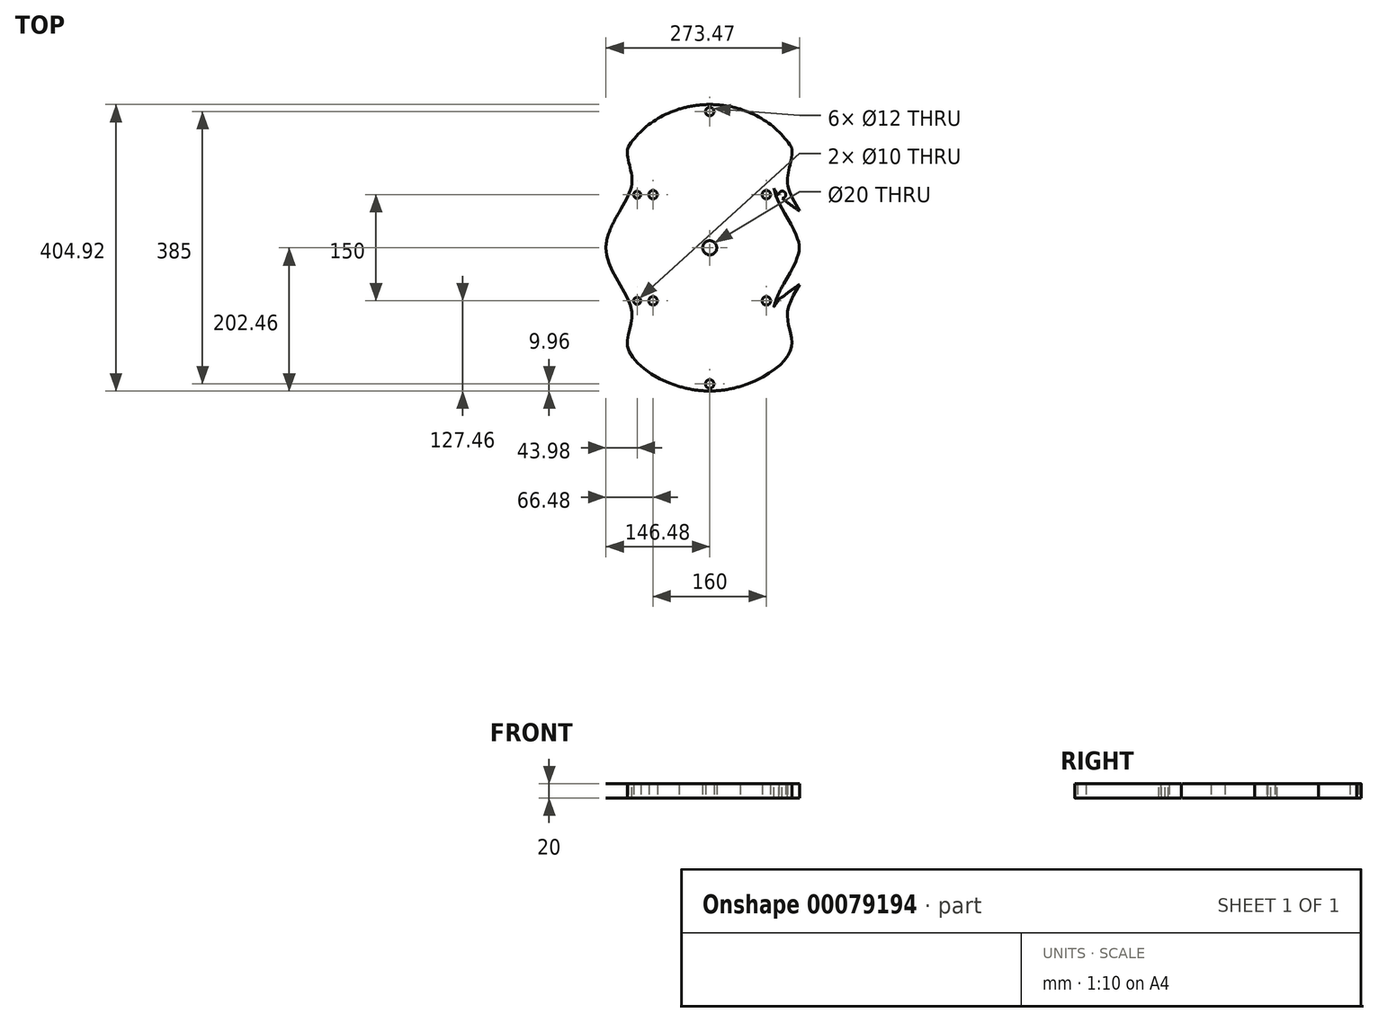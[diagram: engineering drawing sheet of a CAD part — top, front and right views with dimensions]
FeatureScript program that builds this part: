
annotation { "Feature Type Name" : "Feature", "Feature Type Description" : "" }
export const myFeature = defineFeature(function(context is Context, id is Id, definition is map)
    precondition{}
    {
        {
            var Q0;
            Q0=qCreatedBy(makeId("Top.planeOp"),FACE);
            var sketch = newSketch(context, id + "F0", { "sketchPlane" : qUnion([Q0])});
            skPoint(sketch, "E0", {"position": v(150.32, -165.76) * mm});
            skPoint(sketch, "E1", {"position": v(107.37, -221.56) * mm});
            skPoint(sketch, "E2", {"position": v(69.02, -211.72) * mm});
            skPoint(sketch, "E3", {"position": v(0, -246.18) * mm});
            skPoint(sketch, "E4", {"position": v(138.05, -177.25) * mm});
            skPoint(sketch, "E5", {"position": v(146.48, 0) * mm});
            skPoint(sketch, "E6", {"position": v(132.68, -82.88) * mm});
            skLineSegment(sketch, "E7", {"start": v(0, 292) * mm, "end": v(0, -246.18) * mm, "construction": true});
            skPoint(sketch, "E8.MirrorP", {"position": v(-146.48, 0) * mm});
            skPoint(sketch, "E9.MirrorP", {"position": v(-132.68, -82.88) * mm});
            skPoint(sketch, "E10.MirrorP", {"position": v(-150.32, -165.76) * mm});
            skPoint(sketch, "E11.MirrorP", {"position": v(-138.05, -177.25) * mm});
            skPoint(sketch, "E12.MirrorP", {"position": v(-107.37, -221.56) * mm});
            skPoint(sketch, "E13.MirrorP", {"position": v(-69.02, -211.72) * mm});
            skPoint(sketch, "E14", {"position": v(0, 0) * mm});
            skPoint(sketch, "E15", {"position": v(-146.25, -161.4) * mm});
            skPoint(sketch, "E16", {"position": v(-136.87, -189.28) * mm});
            skPoint(sketch, "E17", {"position": v(-146.26, -172.33) * mm});
            skPoint(sketch, "E18", {"position": v(-131.04, -210.06) * mm});
            skPoint(sketch, "E19", {"position": v(-94.82, -218.38) * mm});
            skPoint(sketch, "E20", {"position": v(-60.59, -222.84) * mm});
            skPoint(sketch, "E21", {"position": v(-67.25, -214.49) * mm});
            skPoint(sketch, "E22", {"position": v(-72.48, -210.2) * mm});
            skPoint(sketch, "E23", {"position": v(-119.37, -219.05) * mm});
            skPoint(sketch, "E24", {"position": v(-149.89, -167.68) * mm});
            skPoint(sketch, "E25.MirrorP", {"position": v(60.59, -222.84) * mm});
            skPoint(sketch, "E26.MirrorP", {"position": v(67.25, -214.49) * mm});
            skPoint(sketch, "E27.MirrorP", {"position": v(72.48, -210.2) * mm});
            skPoint(sketch, "E28.MirrorP", {"position": v(94.82, -218.38) * mm});
            skPoint(sketch, "E29.MirrorP", {"position": v(119.37, -219.05) * mm});
            skPoint(sketch, "E30.MirrorP", {"position": v(136.87, -189.28) * mm});
            skPoint(sketch, "E31.MirrorP", {"position": v(146.26, -172.33) * mm});
            skPoint(sketch, "E32.MirrorP", {"position": v(149.89, -167.68) * mm});
            skPoint(sketch, "E33.MirrorP", {"position": v(146.25, -161.4) * mm});
            skPoint(sketch, "E34", {"position": v(-139.73, -175.31) * mm});
            skPoint(sketch, "E35.MirrorP", {"position": v(131.04, -210.06) * mm});
            skPoint(sketch, "E36.MirrorP", {"position": v(-132.68, 82.88) * mm});
            skPoint(sketch, "E37.MirrorP", {"position": v(-139.73, 175.31) * mm});
            skPoint(sketch, "E38.MirrorP", {"position": v(-150.32, 165.76) * mm});
            skPoint(sketch, "E39.MirrorP", {"position": v(69.02, 211.72) * mm});
            skPoint(sketch, "E40.MirrorP", {"position": v(150.32, 165.76) * mm});
            skPoint(sketch, "E41.MirrorP", {"position": v(-67.25, 214.49) * mm});
            skPoint(sketch, "E42.MirrorP", {"position": v(131.04, 210.06) * mm});
            skPoint(sketch, "E43.MirrorP", {"position": v(60.59, 222.84) * mm});
            skPoint(sketch, "E44.MirrorP", {"position": v(119.37, 219.05) * mm});
            skPoint(sketch, "E45.MirrorP", {"position": v(136.87, 189.28) * mm});
            skPoint(sketch, "E46.MirrorP", {"position": v(-72.48, 210.2) * mm});
            skPoint(sketch, "E47.MirrorP", {"position": v(-138.05, 177.25) * mm});
            skPoint(sketch, "E48.MirrorP", {"position": v(-69.02, 211.72) * mm});
            skPoint(sketch, "E49.MirrorP", {"position": v(72.48, 210.2) * mm});
            skPoint(sketch, "E50.MirrorP", {"position": v(-146.25, 161.4) * mm});
            skPoint(sketch, "E51.MirrorP", {"position": v(-136.87, 189.28) * mm});
            skPoint(sketch, "E52.MirrorP", {"position": v(138.05, 177.25) * mm});
            skPoint(sketch, "E53.MirrorP", {"position": v(67.25, 214.49) * mm});
            skPoint(sketch, "E54.MirrorP", {"position": v(-149.89, 167.68) * mm});
            skPoint(sketch, "E55.MirrorP", {"position": v(149.89, 167.68) * mm});
            skPoint(sketch, "E56.MirrorP", {"position": v(-107.37, 221.56) * mm});
            skPoint(sketch, "E57.MirrorP", {"position": v(-94.82, 218.38) * mm});
            skPoint(sketch, "E58.MirrorP", {"position": v(146.26, 172.33) * mm});
            skPoint(sketch, "E59.MirrorP", {"position": v(107.37, 221.56) * mm});
            skPoint(sketch, "E60.MirrorP", {"position": v(-131.04, 210.06) * mm});
            skPoint(sketch, "E61.MirrorP", {"position": v(94.82, 218.38) * mm});
            skPoint(sketch, "E62.MirrorP", {"position": v(146.25, 161.4) * mm});
            skPoint(sketch, "E63.MirrorP", {"position": v(0, 246.18) * mm});
            skPoint(sketch, "E64.MirrorP", {"position": v(-146.26, 172.33) * mm});
            skPoint(sketch, "E65.MirrorP", {"position": v(-119.37, 219.05) * mm});
            skPoint(sketch, "E66.MirrorP", {"position": v(-60.59, 222.84) * mm});
            skPoint(sketch, "E67.MirrorP", {"position": v(132.68, 82.88) * mm});
            skFitSpline(sketch, "E68", {"points": [v(-146.48, 0) * mm, v(-132.68, 82.88) * mm, v(-146.25, 161.4) * mm, v(-150.32, 165.76) * mm, v(-149.89, 167.68) * mm, v(-146.26, 172.33) * mm, v(-139.73, 175.31) * mm, v(-138.05, 177.25) * mm, v(-136.87, 189.28) * mm, v(-131.04, 210.06) * mm, v(-119.37, 219.05) * mm, v(-107.37, 221.56) * mm, v(-94.82, 218.38) * mm, v(-72.48, 210.2) * mm, v(-69.02, 211.72) * mm, v(-67.25, 214.49) * mm, v(-60.59, 222.84) * mm, v(0, 246.18) * mm, v(60.59, 222.84) * mm, v(67.25, 214.49) * mm, v(69.02, 211.72) * mm, v(72.48, 210.2) * mm, v(94.82, 218.38) * mm, v(107.37, 221.56) * mm, v(119.37, 219.05) * mm, v(131.04, 210.06) * mm, v(136.87, 189.28) * mm, v(138.05, 177.25) * mm, v(146.26, 172.33) * mm, v(149.89, 167.68) * mm, v(150.32, 165.76) * mm, v(146.25, 161.4) * mm, v(132.68, 82.88) * mm, v(146.48, 0) * mm, v(132.68, -82.88) * mm, v(146.25, -161.4) * mm, v(150.32, -165.76) * mm, v(149.89, -167.68) * mm, v(146.26, -172.33) * mm, v(138.05, -177.25) * mm, v(136.87, -189.28) * mm, v(131.04, -210.06) * mm, v(119.37, -219.05) * mm, v(107.37, -221.56) * mm, v(94.82, -218.38) * mm, v(72.48, -210.2) * mm, v(69.02, -211.72) * mm, v(67.25, -214.49) * mm, v(60.59, -222.84) * mm, v(0, -246.18) * mm, v(-60.59, -222.84) * mm, v(-67.25, -214.49) * mm, v(-69.02, -211.72) * mm, v(-72.48, -210.2) * mm, v(-94.82, -218.38) * mm, v(-107.37, -221.56) * mm, v(-119.37, -219.05) * mm, v(-131.04, -210.06) * mm, v(-136.87, -189.28) * mm, v(-138.05, -177.25) * mm, v(-139.73, -175.31) * mm, v(-146.26, -172.33) * mm, v(-149.89, -167.68) * mm, v(-150.32, -165.76) * mm, v(-146.25, -161.4) * mm, v(-132.68, -82.88) * mm, v(-146.48, 0) * mm]});
            skPoint(sketch, "E69", {"position": v(0, 295) * mm});
            skPoint(sketch, "E70", {"position": v(-30, 295) * mm});
            skPoint(sketch, "E71", {"position": v(-225, 0) * mm});
            skPoint(sketch, "E72", {"position": v(-225, 100) * mm});
            skPoint(sketch, "E73.MirrorP", {"position": v(225, 100) * mm});
            skPoint(sketch, "E74.MirrorP", {"position": v(225, -60) * mm});
            skLineSegment(sketch, "E75", {"start": v(0, 0) * mm, "end": v(-373.3, 215.53) * mm, "construction": true});
            skLineSegment(sketch, "E76", {"start": v(0, 0) * mm, "end": v(-204.64, 354.44) * mm, "construction": true});
            skLineSegment(sketch, "E77", {"start": v(-225, 0) * mm, "end": v(-225, 100) * mm});
            skLineSegment(sketch, "E78", {"start": v(-30, 295) * mm, "end": v(0, 295) * mm});
            skPoint(sketch, "E79", {"position": v(-30, 100) * mm});
            skArc(sketch, "E80", {"start": v(-30, 295) * mm, "mid": v(-167.89, 237.89) * mm, "end": v(-225, 100) * mm});
            skLineSegment(sketch, "E81.MirrorCS", {"start": v(225, 0) * mm, "end": v(225, 100) * mm});
            skArc(sketch, "E82.MirrorCS", {"start": v(30, 295) * mm, "mid": v(167.89, 237.89) * mm, "end": v(225, 100) * mm});
            skLineSegment(sketch, "E83.MirrorCS", {"start": v(30, 295) * mm, "end": v(0, 295) * mm});
            skArc(sketch, "E84.MirrorCS", {"start": v(-30, -295) * mm, "mid": v(-167.89, -237.89) * mm, "end": v(-225, -100) * mm});
            skLineSegment(sketch, "E85.MirrorCS", {"start": v(-225, 0) * mm, "end": v(-225, -100) * mm});
            skLineSegment(sketch, "E86.MirrorCS", {"start": v(225, 0) * mm, "end": v(225, -100) * mm});
            skArc(sketch, "E87.MirrorCS", {"start": v(30, -295) * mm, "mid": v(167.89, -237.89) * mm, "end": v(225, -100) * mm});
            skLineSegment(sketch, "E88.MirrorCS", {"start": v(30, -295) * mm, "end": v(0, -295) * mm});
            skLineSegment(sketch, "E89.MirrorCS", {"start": v(-30, -295) * mm, "end": v(0, -295) * mm});
            skEllipse(sketch, "E90", {"center": v(0, 82.88) * mm, "majorRadius": 132.68 * mm, "minorRadius": 119.58 * mm, "majorAxis": v(1, 0)});
            skCircle(sketch, "E91", {"center": v(102.5, 75) * mm, "radius": 5 * mm});
            skCircle(sketch, "E92.MirrorC", {"center": v(-102.5, 75) * mm, "radius": 5 * mm});
            skCircle(sketch, "E93.MirrorC", {"center": v(102.5, -75) * mm, "radius": 5 * mm});
            skCircle(sketch, "E94.MirrorC", {"center": v(-102.5, -75) * mm, "radius": 5 * mm});
            skSolve(sketch);
        }
        {
            var Q0;
            {var subQ0=sQuery(id+"F0.wireOp",EDGE,"E90");var subQ1=sQuery(id+"F0.wireOp",EDGE,"E68");var subQ2=makeQuery(id+"F0.imprint","INTERSECT",VERTEX,{"disambiguationData":[OD(0.0)],"derivedFrom":[subQ1,subQ0]});Q0=makeQuery(id+"F0.imprint","IMPRINT",FACE,{"disambiguationData":[TD([[makeQuery(id+"F0.imprint","IMPRINT",EDGE,{"disambiguationData":[TD([[subQ2,1.0]])],"derivedFrom":subQ1}),-1.0]])]});}
            var sketch = newSketch(context, id + "F1", { "sketchPlane" : qUnion([Q0])});
            skFitSpline(sketch, "E95.0", {"points": [v(-146.48, 0) * mm, v(-146.48, 25.45) * mm, v(-122.55, 75.68) * mm, v(-141.58, 161.6) * mm, v(-150.97, 165.24) * mm, v(-149.84, 167.93) * mm, v(-146.88, 173.13) * mm, v(-139.54, 174.98) * mm, v(-137.39, 177.3) * mm, v(-137.38, 190.15) * mm, v(-133.28, 211.38) * mm, v(-119.9, 219.69) * mm, v(-106.83, 222.51) * mm, v(-95.46, 219.19) * mm, v(-72.9, 208.32) * mm, v(-68.89, 211.56) * mm, v(-66.98, 214.97) * mm, v(-60.9, 225.94) * mm, v(0, 260.58) * mm, v(60.9, 225.94) * mm, v(66.98, 214.97) * mm, v(68.89, 211.56) * mm, v(72.9, 208.32) * mm, v(95.47, 219.19) * mm, v(106.82, 222.52) * mm, v(119.95, 219.67) * mm, v(133.09, 211.44) * mm, v(138.2, 189.9) * mm, v(135.3, 175.97) * mm, v(146.9, 173.38) * mm, v(149.81, 167.94) * mm, v(150.98, 165.24) * mm, v(141.57, 161.6) * mm, v(122.55, 75.68) * mm, v(158.6, 0) * mm, v(122.55, -75.68) * mm, v(141.57, -161.6) * mm, v(150.98, -165.24) * mm, v(149.81, -167.94) * mm, v(146.9, -173.38) * mm, v(135.3, -175.97) * mm, v(138.2, -189.9) * mm, v(133.09, -211.44) * mm, v(119.95, -219.67) * mm, v(106.82, -222.52) * mm, v(95.47, -219.19) * mm, v(72.9, -208.32) * mm, v(68.89, -211.56) * mm, v(66.98, -214.97) * mm, v(60.9, -225.94) * mm, v(0, -260.58) * mm, v(-60.9, -225.94) * mm, v(-66.98, -214.97) * mm, v(-68.89, -211.56) * mm, v(-72.9, -208.32) * mm, v(-95.46, -219.19) * mm, v(-106.83, -222.51) * mm, v(-119.9, -219.69) * mm, v(-133.28, -211.38) * mm, v(-137.38, -190.15) * mm, v(-137.39, -177.3) * mm, v(-139.54, -174.98) * mm, v(-146.88, -173.13) * mm, v(-149.84, -167.93) * mm, v(-150.97, -165.24) * mm, v(-141.58, -161.6) * mm, v(-122.55, -75.68) * mm, v(-146.48, -25.45) * mm, v(-146.48, 0) * mm]});
            skEllipticalArc(sketch, "E96.0", {});
            skEllipticalArc(sketch, "E97.MirrorC", {});
            skFitSpline(sketch, "E98.trimOffspring", {"points": [v(-146.48, 0) * mm, v(-146.48, 25.45) * mm, v(-122.55, 75.68) * mm, v(-141.58, 161.6) * mm, v(-150.97, 165.24) * mm, v(-149.84, 167.93) * mm, v(-146.88, 173.13) * mm, v(-139.54, 174.98) * mm, v(-137.39, 177.3) * mm, v(-137.38, 190.15) * mm, v(-133.28, 211.38) * mm, v(-119.9, 219.69) * mm, v(-106.83, 222.51) * mm, v(-95.46, 219.19) * mm, v(-72.9, 208.32) * mm, v(-68.89, 211.56) * mm, v(-66.98, 214.97) * mm, v(-60.9, 225.94) * mm, v(0, 260.58) * mm, v(60.9, 225.94) * mm, v(66.98, 214.97) * mm, v(68.89, 211.56) * mm, v(72.9, 208.32) * mm, v(95.47, 219.19) * mm, v(106.82, 222.52) * mm, v(119.95, 219.67) * mm, v(133.09, 211.44) * mm, v(138.2, 189.9) * mm, v(135.3, 175.97) * mm, v(146.9, 173.38) * mm, v(149.81, 167.94) * mm, v(150.98, 165.24) * mm, v(141.57, 161.6) * mm, v(122.55, 75.68) * mm, v(158.6, 0) * mm, v(122.55, -75.68) * mm, v(141.57, -161.6) * mm, v(150.98, -165.24) * mm, v(149.81, -167.94) * mm, v(146.9, -173.38) * mm, v(135.3, -175.97) * mm, v(138.2, -189.9) * mm, v(133.09, -211.44) * mm, v(119.95, -219.67) * mm, v(106.82, -222.52) * mm, v(95.47, -219.19) * mm, v(72.9, -208.32) * mm, v(68.89, -211.56) * mm, v(66.98, -214.97) * mm, v(60.9, -225.94) * mm, v(0, -260.58) * mm, v(-60.9, -225.94) * mm, v(-66.98, -214.97) * mm, v(-68.89, -211.56) * mm, v(-72.9, -208.32) * mm, v(-95.46, -219.19) * mm, v(-106.83, -222.51) * mm, v(-119.9, -219.69) * mm, v(-133.28, -211.38) * mm, v(-137.38, -190.15) * mm, v(-137.39, -177.3) * mm, v(-139.54, -174.98) * mm, v(-146.88, -173.13) * mm, v(-149.84, -167.93) * mm, v(-150.97, -165.24) * mm, v(-141.58, -161.6) * mm, v(-122.55, -75.68) * mm, v(-146.48, -25.45) * mm, v(-146.48, 0) * mm]});
            skPoint(sketch, "E99", {"position": v(0, 202.46) * mm});
            skPoint(sketch, "E100", {"position": v(-110, 90) * mm});
            skPoint(sketch, "E101", {"position": v(-115, 143) * mm});
            skPoint(sketch, "E102.MirrorP", {"position": v(115, 143) * mm});
            skPoint(sketch, "E103.MirrorP", {"position": v(110, 90) * mm});
            skPoint(sketch, "E104.MirrorP", {"position": v(-110, -90) * mm});
            skPoint(sketch, "E105.MirrorP", {"position": v(-115, -143) * mm});
            skPoint(sketch, "E106.MirrorP", {"position": v(0, -202.46) * mm});
            skPoint(sketch, "E107.MirrorP", {"position": v(115, -143) * mm});
            skPoint(sketch, "E108.MirrorP", {"position": v(110, -90) * mm});
            skFitSpline(sketch, "E109", {"points": [v(-146.48, 0) * mm, v(-110, 90) * mm, v(-115, 143) * mm, v(0, 202.46) * mm, v(115, 143) * mm, v(110, 90) * mm, v(146.48, 0) * mm, v(110, -90) * mm, v(115, -143) * mm, v(0, -202.46) * mm, v(-115, -143) * mm, v(-110, -90) * mm, v(-146.48, 0) * mm]});
            skFitSpline(sketch, "E110.trimOffspring", {"points": [v(-146.48, 0) * mm, v(-146.48, 25.45) * mm, v(-122.55, 75.68) * mm, v(-141.58, 161.6) * mm, v(-150.97, 165.24) * mm, v(-149.84, 167.93) * mm, v(-146.88, 173.13) * mm, v(-139.54, 174.98) * mm, v(-137.39, 177.3) * mm, v(-137.38, 190.15) * mm, v(-133.28, 211.38) * mm, v(-119.9, 219.69) * mm, v(-106.83, 222.51) * mm, v(-95.46, 219.19) * mm, v(-72.9, 208.32) * mm, v(-68.89, 211.56) * mm, v(-66.98, 214.97) * mm, v(-60.9, 225.94) * mm, v(0, 260.58) * mm, v(60.9, 225.94) * mm, v(66.98, 214.97) * mm, v(68.89, 211.56) * mm, v(72.9, 208.32) * mm, v(95.47, 219.19) * mm, v(106.82, 222.52) * mm, v(119.95, 219.67) * mm, v(133.09, 211.44) * mm, v(138.2, 189.9) * mm, v(135.3, 175.97) * mm, v(146.9, 173.38) * mm, v(149.81, 167.94) * mm, v(150.98, 165.24) * mm, v(141.57, 161.6) * mm, v(122.55, 75.68) * mm, v(158.6, 0) * mm, v(122.55, -75.68) * mm, v(141.57, -161.6) * mm, v(150.98, -165.24) * mm, v(149.81, -167.94) * mm, v(146.9, -173.38) * mm, v(135.3, -175.97) * mm, v(138.2, -189.9) * mm, v(133.09, -211.44) * mm, v(119.95, -219.67) * mm, v(106.82, -222.52) * mm, v(95.47, -219.19) * mm, v(72.9, -208.32) * mm, v(68.89, -211.56) * mm, v(66.98, -214.97) * mm, v(60.9, -225.94) * mm, v(0, -260.58) * mm, v(-60.9, -225.94) * mm, v(-66.98, -214.97) * mm, v(-68.89, -211.56) * mm, v(-72.9, -208.32) * mm, v(-95.46, -219.19) * mm, v(-106.83, -222.51) * mm, v(-119.9, -219.69) * mm, v(-133.28, -211.38) * mm, v(-137.38, -190.15) * mm, v(-137.39, -177.3) * mm, v(-139.54, -174.98) * mm, v(-146.88, -173.13) * mm, v(-149.84, -167.93) * mm, v(-150.97, -165.24) * mm, v(-141.58, -161.6) * mm, v(-122.55, -75.68) * mm, v(-146.48, -25.45) * mm, v(-146.48, 0) * mm]});
            skFitSpline(sketch, "E111.trimOffspring", {"points": [v(-146.48, 0) * mm, v(-146.48, 25.45) * mm, v(-122.55, 75.68) * mm, v(-141.58, 161.6) * mm, v(-150.97, 165.24) * mm, v(-149.84, 167.93) * mm, v(-146.88, 173.13) * mm, v(-139.54, 174.98) * mm, v(-137.39, 177.3) * mm, v(-137.38, 190.15) * mm, v(-133.28, 211.38) * mm, v(-119.9, 219.69) * mm, v(-106.83, 222.51) * mm, v(-95.46, 219.19) * mm, v(-72.9, 208.32) * mm, v(-68.89, 211.56) * mm, v(-66.98, 214.97) * mm, v(-60.9, 225.94) * mm, v(0, 260.58) * mm, v(60.9, 225.94) * mm, v(66.98, 214.97) * mm, v(68.89, 211.56) * mm, v(72.9, 208.32) * mm, v(95.47, 219.19) * mm, v(106.82, 222.52) * mm, v(119.95, 219.67) * mm, v(133.09, 211.44) * mm, v(138.2, 189.9) * mm, v(135.3, 175.97) * mm, v(146.9, 173.38) * mm, v(149.81, 167.94) * mm, v(150.98, 165.24) * mm, v(141.57, 161.6) * mm, v(122.55, 75.68) * mm, v(158.6, 0) * mm, v(122.55, -75.68) * mm, v(141.57, -161.6) * mm, v(150.98, -165.24) * mm, v(149.81, -167.94) * mm, v(146.9, -173.38) * mm, v(135.3, -175.97) * mm, v(138.2, -189.9) * mm, v(133.09, -211.44) * mm, v(119.95, -219.67) * mm, v(106.82, -222.52) * mm, v(95.47, -219.19) * mm, v(72.9, -208.32) * mm, v(68.89, -211.56) * mm, v(66.98, -214.97) * mm, v(60.9, -225.94) * mm, v(0, -260.58) * mm, v(-60.9, -225.94) * mm, v(-66.98, -214.97) * mm, v(-68.89, -211.56) * mm, v(-72.9, -208.32) * mm, v(-95.46, -219.19) * mm, v(-106.83, -222.51) * mm, v(-119.9, -219.69) * mm, v(-133.28, -211.38) * mm, v(-137.38, -190.15) * mm, v(-137.39, -177.3) * mm, v(-139.54, -174.98) * mm, v(-146.88, -173.13) * mm, v(-149.84, -167.93) * mm, v(-150.97, -165.24) * mm, v(-141.58, -161.6) * mm, v(-122.55, -75.68) * mm, v(-146.48, -25.45) * mm, v(-146.48, 0) * mm]});
            skFitSpline(sketch, "E112.trimOffspring", {"points": [v(-146.48, 0) * mm, v(-146.48, 25.45) * mm, v(-122.55, 75.68) * mm, v(-141.58, 161.6) * mm, v(-150.97, 165.24) * mm, v(-149.84, 167.93) * mm, v(-146.88, 173.13) * mm, v(-139.54, 174.98) * mm, v(-137.39, 177.3) * mm, v(-137.38, 190.15) * mm, v(-133.28, 211.38) * mm, v(-119.9, 219.69) * mm, v(-106.83, 222.51) * mm, v(-95.46, 219.19) * mm, v(-72.9, 208.32) * mm, v(-68.89, 211.56) * mm, v(-66.98, 214.97) * mm, v(-60.9, 225.94) * mm, v(0, 260.58) * mm, v(60.9, 225.94) * mm, v(66.98, 214.97) * mm, v(68.89, 211.56) * mm, v(72.9, 208.32) * mm, v(95.47, 219.19) * mm, v(106.82, 222.52) * mm, v(119.95, 219.67) * mm, v(133.09, 211.44) * mm, v(138.2, 189.9) * mm, v(135.3, 175.97) * mm, v(146.9, 173.38) * mm, v(149.81, 167.94) * mm, v(150.98, 165.24) * mm, v(141.57, 161.6) * mm, v(122.55, 75.68) * mm, v(158.6, 0) * mm, v(122.55, -75.68) * mm, v(141.57, -161.6) * mm, v(150.98, -165.24) * mm, v(149.81, -167.94) * mm, v(146.9, -173.38) * mm, v(135.3, -175.97) * mm, v(138.2, -189.9) * mm, v(133.09, -211.44) * mm, v(119.95, -219.67) * mm, v(106.82, -222.52) * mm, v(95.47, -219.19) * mm, v(72.9, -208.32) * mm, v(68.89, -211.56) * mm, v(66.98, -214.97) * mm, v(60.9, -225.94) * mm, v(0, -260.58) * mm, v(-60.9, -225.94) * mm, v(-66.98, -214.97) * mm, v(-68.89, -211.56) * mm, v(-72.9, -208.32) * mm, v(-95.46, -219.19) * mm, v(-106.83, -222.51) * mm, v(-119.9, -219.69) * mm, v(-133.28, -211.38) * mm, v(-137.38, -190.15) * mm, v(-137.39, -177.3) * mm, v(-139.54, -174.98) * mm, v(-146.88, -173.13) * mm, v(-149.84, -167.93) * mm, v(-150.97, -165.24) * mm, v(-141.58, -161.6) * mm, v(-122.55, -75.68) * mm, v(-146.48, -25.45) * mm, v(-146.48, 0) * mm]});
            skEllipticalArc(sketch, "E113.trimOffspring", {});
            skEllipticalArc(sketch, "E114.trimOffspring", {});
            skEllipticalArc(sketch, "E115.trimOffspring", {});
            skEllipticalArc(sketch, "E116.trimOffspring", {});
            skCircle(sketch, "E117", {"center": v(0, 192.5) * mm, "radius": 6 * mm});
            skLineSegment(sketch, "E118", {"start": v(-226.31, 0) * mm, "end": v(229.86, 0) * mm, "construction": true});
            skCircle(sketch, "E119.MirrorC", {"center": v(0, -192.5) * mm, "radius": 6 * mm});
            skPoint(sketch, "E120", {"position": v(-80, 75) * mm});
            skCircle(sketch, "E121", {"center": v(-80, 75) * mm, "radius": 6 * mm});
            skFitSpline(sketch, "E122.0", {"points": [v(-126.48, -0.62) * mm, v(-126.48, 0) * mm, v(-126.48, 0.62) * mm, v(-126.45, 1.48) * mm, v(-126.37, 2.57) * mm, v(-126.23, 3.92) * mm, v(-125.95, 5.8) * mm, v(-125.44, 8.25) * mm, v(-124.57, 11.4) * mm, v(-123.44, 14.7) * mm, v(-121.62, 19.33) * mm, v(-118.77, 25.43) * mm, v(-114.67, 33.14) * mm, v(-110.1, 41.14) * mm, v(-105.34, 49.38) * mm, v(-101.43, 56.47) * mm, v(-98.47, 62.31) * mm, v(-96.37, 66.81) * mm, v(-94.44, 71.44) * mm, v(-93, 75.45) * mm, v(-92, 78.76) * mm, v(-91.33, 81.3) * mm, v(-90.75, 83.9) * mm, v(-90.35, 86.12) * mm, v(-90.1, 87.93) * mm, v(-89.88, 89.73) * mm, v(-89.7, 91.94) * mm, v(-89.6, 94.53) * mm, v(-89.61, 97.06) * mm, v(-89.72, 99.51) * mm, v(-89.98, 102.68) * mm, v(-90.47, 106.44) * mm, v(-91.26, 110.63) * mm, v(-92.14, 114.5) * mm, v(-93.04, 118.06) * mm, v(-94.2, 122.4) * mm, v(-95.17, 126.15) * mm, v(-95.82, 129.29) * mm, v(-96.14, 131.32) * mm, v(-96.3, 133.04) * mm, v(-96.31, 134.46) * mm, v(-96.23, 135.45) * mm, v(-96.11, 136.18) * mm, v(-96.02, 136.62) * mm, v(-95.93, 136.97) * mm, v(-95.85, 137.24) * mm, v(-95.76, 137.52) * mm, v(-95.62, 137.93) * mm, v(-95.4, 138.5) * mm, v(-94.93, 139.51) * mm, v(-94.14, 140.98) * mm, v(-92.83, 143) * mm, v(-91.14, 145.21) * mm, v(-89.1, 147.56) * mm, v(-86.7, 150.02) * mm, v(-83.04, 153.37) * mm, v(-77.67, 157.62) * mm, v(-70.12, 162.62) * mm, v(-61.63, 167.33) * mm, v(-52.35, 171.62) * mm, v(-42.46, 175.35) * mm, v(-32.12, 178.4) * mm, v(-23.26, 180.32) * mm, v(-16.1, 181.41) * mm, v(-10.72, 182.01) * mm, v(-6.24, 182.32) * mm, v(-2.67, 182.44) * mm, v(0, 182.47) * mm, v(2.67, 182.44) * mm, v(6.24, 182.32) * mm, v(10.72, 182.01) * mm, v(16.1, 181.41) * mm, v(23.26, 180.32) * mm, v(32.12, 178.4) * mm, v(42.46, 175.35) * mm, v(52.35, 171.62) * mm, v(61.63, 167.33) * mm, v(70.12, 162.62) * mm, v(77.67, 157.62) * mm, v(83.04, 153.37) * mm, v(86.7, 150.02) * mm, v(89.1, 147.56) * mm, v(91.14, 145.21) * mm, v(92.83, 143) * mm, v(94.14, 140.98) * mm, v(94.93, 139.51) * mm, v(95.4, 138.5) * mm, v(95.62, 137.93) * mm, v(95.76, 137.52) * mm, v(95.85, 137.24) * mm, v(95.93, 136.97) * mm, v(96.02, 136.62) * mm, v(96.11, 136.18) * mm, v(96.23, 135.45) * mm, v(96.31, 134.46) * mm, v(96.3, 133.04) * mm, v(96.14, 131.32) * mm, v(95.82, 129.29) * mm, v(95.17, 126.15) * mm, v(94.2, 122.4) * mm, v(93.04, 118.06) * mm, v(92.14, 114.5) * mm, v(91.26, 110.63) * mm, v(90.47, 106.44) * mm, v(89.98, 102.68) * mm, v(89.72, 99.51) * mm, v(89.61, 97.06) * mm, v(89.6, 94.53) * mm, v(89.7, 91.94) * mm, v(89.88, 89.73) * mm, v(90.1, 87.93) * mm, v(90.35, 86.12) * mm, v(90.75, 83.9) * mm, v(91.33, 81.3) * mm, v(92, 78.76) * mm, v(93, 75.45) * mm, v(94.44, 71.44) * mm, v(96.37, 66.81) * mm, v(98.47, 62.31) * mm, v(101.43, 56.47) * mm, v(105.34, 49.38) * mm, v(110.1, 41.14) * mm, v(114.67, 33.14) * mm, v(118.77, 25.43) * mm, v(121.62, 19.33) * mm, v(123.44, 14.7) * mm, v(124.57, 11.4) * mm, v(125.44, 8.25) * mm, v(125.95, 5.8) * mm, v(126.23, 3.92) * mm, v(126.37, 2.57) * mm, v(126.45, 1.48) * mm, v(126.48, 0.62) * mm, v(126.48, 0) * mm, v(126.48, -0.62) * mm, v(126.45, -1.48) * mm, v(126.37, -2.57) * mm, v(126.23, -3.92) * mm, v(125.95, -5.8) * mm, v(125.44, -8.25) * mm, v(124.57, -11.4) * mm, v(123.44, -14.7) * mm, v(121.62, -19.33) * mm, v(118.77, -25.43) * mm, v(114.67, -33.14) * mm, v(110.1, -41.14) * mm, v(105.34, -49.38) * mm, v(101.43, -56.47) * mm, v(98.47, -62.31) * mm, v(96.37, -66.81) * mm, v(94.44, -71.44) * mm, v(93, -75.45) * mm, v(92, -78.76) * mm, v(91.33, -81.3) * mm, v(90.75, -83.9) * mm, v(90.35, -86.12) * mm, v(90.1, -87.93) * mm, v(89.88, -89.73) * mm, v(89.7, -91.94) * mm, v(89.6, -94.53) * mm, v(89.61, -97.06) * mm, v(89.72, -99.51) * mm, v(89.98, -102.68) * mm, v(90.47, -106.44) * mm, v(91.26, -110.63) * mm, v(92.14, -114.5) * mm, v(93.04, -118.06) * mm, v(94.2, -122.4) * mm, v(95.17, -126.15) * mm, v(95.82, -129.29) * mm, v(96.14, -131.32) * mm, v(96.3, -133.04) * mm, v(96.31, -134.46) * mm, v(96.23, -135.45) * mm, v(96.11, -136.18) * mm, v(96.02, -136.62) * mm, v(95.93, -136.97) * mm, v(95.85, -137.24) * mm, v(95.76, -137.52) * mm, v(95.62, -137.93) * mm, v(95.4, -138.5) * mm, v(94.93, -139.51) * mm, v(94.14, -140.98) * mm, v(92.83, -143) * mm, v(91.14, -145.21) * mm, v(89.1, -147.56) * mm, v(86.7, -150.02) * mm, v(83.04, -153.37) * mm, v(77.67, -157.62) * mm, v(70.12, -162.62) * mm, v(61.63, -167.33) * mm, v(52.35, -171.62) * mm, v(42.46, -175.35) * mm, v(32.12, -178.4) * mm, v(23.26, -180.32) * mm, v(16.1, -181.41) * mm, v(10.72, -182.01) * mm, v(6.24, -182.32) * mm, v(2.67, -182.44) * mm, v(0, -182.47) * mm, v(-2.67, -182.44) * mm, v(-6.24, -182.32) * mm, v(-10.72, -182.01) * mm, v(-16.1, -181.41) * mm, v(-23.26, -180.32) * mm, v(-32.12, -178.4) * mm, v(-42.46, -175.35) * mm, v(-52.35, -171.62) * mm, v(-61.63, -167.33) * mm, v(-70.12, -162.62) * mm, v(-77.67, -157.62) * mm, v(-83.04, -153.37) * mm, v(-86.7, -150.02) * mm, v(-89.1, -147.56) * mm, v(-91.14, -145.21) * mm, v(-92.83, -143) * mm, v(-94.14, -140.98) * mm, v(-94.93, -139.51) * mm, v(-95.4, -138.5) * mm, v(-95.62, -137.93) * mm, v(-95.76, -137.52) * mm, v(-95.85, -137.24) * mm, v(-95.93, -136.97) * mm, v(-96.02, -136.62) * mm, v(-96.11, -136.18) * mm, v(-96.23, -135.45) * mm, v(-96.31, -134.46) * mm, v(-96.3, -133.04) * mm, v(-96.14, -131.32) * mm, v(-95.82, -129.29) * mm, v(-95.17, -126.15) * mm, v(-94.2, -122.4) * mm, v(-93.04, -118.06) * mm, v(-92.14, -114.5) * mm, v(-91.26, -110.63) * mm, v(-90.47, -106.44) * mm, v(-89.98, -102.68) * mm, v(-89.72, -99.51) * mm, v(-89.61, -97.06) * mm, v(-89.6, -94.53) * mm, v(-89.7, -91.94) * mm, v(-89.88, -89.73) * mm, v(-90.1, -87.93) * mm, v(-90.35, -86.12) * mm, v(-90.75, -83.9) * mm, v(-91.33, -81.3) * mm, v(-92, -78.76) * mm, v(-93, -75.45) * mm, v(-94.44, -71.44) * mm, v(-96.37, -66.81) * mm, v(-98.47, -62.31) * mm, v(-101.43, -56.47) * mm, v(-105.34, -49.38) * mm, v(-110.1, -41.14) * mm, v(-114.67, -33.14) * mm, v(-118.77, -25.43) * mm, v(-121.62, -19.33) * mm, v(-123.44, -14.7) * mm, v(-124.57, -11.4) * mm, v(-125.44, -8.25) * mm, v(-125.95, -5.8) * mm, v(-126.23, -3.92) * mm, v(-126.37, -2.57) * mm, v(-126.45, -1.48) * mm, v(-126.48, -0.62) * mm, v(-126.48, 0) * mm, v(-126.48, 0.62) * mm]});
            skCircle(sketch, "E123.MirrorC", {"center": v(-80, -75) * mm, "radius": 6 * mm});
            skCircle(sketch, "E124.MirrorC", {"center": v(80, -75) * mm, "radius": 6 * mm});
            skCircle(sketch, "E125.MirrorC", {"center": v(80, 75) * mm, "radius": 6 * mm});
            skFitSpline(sketch, "E126.trimOffspring", {"points": [v(-126.48, -0.62) * mm, v(-126.48, 0) * mm, v(-126.48, 0.62) * mm, v(-126.45, 1.48) * mm, v(-126.37, 2.57) * mm, v(-126.23, 3.92) * mm, v(-125.95, 5.8) * mm, v(-125.44, 8.25) * mm, v(-124.57, 11.4) * mm, v(-123.44, 14.7) * mm, v(-121.62, 19.33) * mm, v(-118.77, 25.43) * mm, v(-114.67, 33.14) * mm, v(-110.1, 41.14) * mm, v(-105.34, 49.38) * mm, v(-101.43, 56.47) * mm, v(-98.47, 62.31) * mm, v(-96.37, 66.81) * mm, v(-94.44, 71.44) * mm, v(-93, 75.45) * mm, v(-92, 78.76) * mm, v(-91.33, 81.3) * mm, v(-90.75, 83.9) * mm, v(-90.35, 86.12) * mm, v(-90.1, 87.93) * mm, v(-89.88, 89.73) * mm, v(-89.7, 91.94) * mm, v(-89.6, 94.53) * mm, v(-89.61, 97.06) * mm, v(-89.72, 99.51) * mm, v(-89.98, 102.68) * mm, v(-90.47, 106.44) * mm, v(-91.26, 110.63) * mm, v(-92.14, 114.5) * mm, v(-93.04, 118.06) * mm, v(-94.2, 122.4) * mm, v(-95.17, 126.15) * mm, v(-95.82, 129.29) * mm, v(-96.14, 131.32) * mm, v(-96.3, 133.04) * mm, v(-96.31, 134.46) * mm, v(-96.23, 135.45) * mm, v(-96.11, 136.18) * mm, v(-96.02, 136.62) * mm, v(-95.93, 136.97) * mm, v(-95.85, 137.24) * mm, v(-95.76, 137.52) * mm, v(-95.62, 137.93) * mm, v(-95.4, 138.5) * mm, v(-94.93, 139.51) * mm, v(-94.14, 140.98) * mm, v(-92.83, 143) * mm, v(-91.14, 145.21) * mm, v(-89.1, 147.56) * mm, v(-86.7, 150.02) * mm, v(-83.04, 153.37) * mm, v(-77.67, 157.62) * mm, v(-70.12, 162.62) * mm, v(-61.63, 167.33) * mm, v(-52.35, 171.62) * mm, v(-42.46, 175.35) * mm, v(-32.12, 178.4) * mm, v(-23.26, 180.32) * mm, v(-16.1, 181.41) * mm, v(-10.72, 182.01) * mm, v(-6.24, 182.32) * mm, v(-2.67, 182.44) * mm, v(0, 182.47) * mm, v(2.67, 182.44) * mm, v(6.24, 182.32) * mm, v(10.72, 182.01) * mm, v(16.1, 181.41) * mm, v(23.26, 180.32) * mm, v(32.12, 178.4) * mm, v(42.46, 175.35) * mm, v(52.35, 171.62) * mm, v(61.63, 167.33) * mm, v(70.12, 162.62) * mm, v(77.67, 157.62) * mm, v(83.04, 153.37) * mm, v(86.7, 150.02) * mm, v(89.1, 147.56) * mm, v(91.14, 145.21) * mm, v(92.83, 143) * mm, v(94.14, 140.98) * mm, v(94.93, 139.51) * mm, v(95.4, 138.5) * mm, v(95.62, 137.93) * mm, v(95.76, 137.52) * mm, v(95.85, 137.24) * mm, v(95.93, 136.97) * mm, v(96.02, 136.62) * mm, v(96.11, 136.18) * mm, v(96.23, 135.45) * mm, v(96.31, 134.46) * mm, v(96.3, 133.04) * mm, v(96.14, 131.32) * mm, v(95.82, 129.29) * mm, v(95.17, 126.15) * mm, v(94.2, 122.4) * mm, v(93.04, 118.06) * mm, v(92.14, 114.5) * mm, v(91.26, 110.63) * mm, v(90.47, 106.44) * mm, v(89.98, 102.68) * mm, v(89.72, 99.51) * mm, v(89.61, 97.06) * mm, v(89.6, 94.53) * mm, v(89.7, 91.94) * mm, v(89.88, 89.73) * mm, v(90.1, 87.93) * mm, v(90.35, 86.12) * mm, v(90.75, 83.9) * mm, v(91.33, 81.3) * mm, v(92, 78.76) * mm, v(93, 75.45) * mm, v(94.44, 71.44) * mm, v(96.37, 66.81) * mm, v(98.47, 62.31) * mm, v(101.43, 56.47) * mm, v(105.34, 49.38) * mm, v(110.1, 41.14) * mm, v(114.67, 33.14) * mm, v(118.77, 25.43) * mm, v(121.62, 19.33) * mm, v(123.44, 14.7) * mm, v(124.57, 11.4) * mm, v(125.44, 8.25) * mm, v(125.95, 5.8) * mm, v(126.23, 3.92) * mm, v(126.37, 2.57) * mm, v(126.45, 1.48) * mm, v(126.48, 0.62) * mm, v(126.48, 0) * mm, v(126.48, -0.62) * mm, v(126.45, -1.48) * mm, v(126.37, -2.57) * mm, v(126.23, -3.92) * mm, v(125.95, -5.8) * mm, v(125.44, -8.25) * mm, v(124.57, -11.4) * mm, v(123.44, -14.7) * mm, v(121.62, -19.33) * mm, v(118.77, -25.43) * mm, v(114.67, -33.14) * mm, v(110.1, -41.14) * mm, v(105.34, -49.38) * mm, v(101.43, -56.47) * mm, v(98.47, -62.31) * mm, v(96.37, -66.81) * mm, v(94.44, -71.44) * mm, v(93, -75.45) * mm, v(92, -78.76) * mm, v(91.33, -81.3) * mm, v(90.75, -83.9) * mm, v(90.35, -86.12) * mm, v(90.1, -87.93) * mm, v(89.88, -89.73) * mm, v(89.7, -91.94) * mm, v(89.6, -94.53) * mm, v(89.61, -97.06) * mm, v(89.72, -99.51) * mm, v(89.98, -102.68) * mm, v(90.47, -106.44) * mm, v(91.26, -110.63) * mm, v(92.14, -114.5) * mm, v(93.04, -118.06) * mm, v(94.2, -122.4) * mm, v(95.17, -126.15) * mm, v(95.82, -129.29) * mm, v(96.14, -131.32) * mm, v(96.3, -133.04) * mm, v(96.31, -134.46) * mm, v(96.23, -135.45) * mm, v(96.11, -136.18) * mm, v(96.02, -136.62) * mm, v(95.93, -136.97) * mm, v(95.85, -137.24) * mm, v(95.76, -137.52) * mm, v(95.62, -137.93) * mm, v(95.4, -138.5) * mm, v(94.93, -139.51) * mm, v(94.14, -140.98) * mm, v(92.83, -143) * mm, v(91.14, -145.21) * mm, v(89.1, -147.56) * mm, v(86.7, -150.02) * mm, v(83.04, -153.37) * mm, v(77.67, -157.62) * mm, v(70.12, -162.62) * mm, v(61.63, -167.33) * mm, v(52.35, -171.62) * mm, v(42.46, -175.35) * mm, v(32.12, -178.4) * mm, v(23.26, -180.32) * mm, v(16.1, -181.41) * mm, v(10.72, -182.01) * mm, v(6.24, -182.32) * mm, v(2.67, -182.44) * mm, v(0, -182.47) * mm, v(-2.67, -182.44) * mm, v(-6.24, -182.32) * mm, v(-10.72, -182.01) * mm, v(-16.1, -181.41) * mm, v(-23.26, -180.32) * mm, v(-32.12, -178.4) * mm, v(-42.46, -175.35) * mm, v(-52.35, -171.62) * mm, v(-61.63, -167.33) * mm, v(-70.12, -162.62) * mm, v(-77.67, -157.62) * mm, v(-83.04, -153.37) * mm, v(-86.7, -150.02) * mm, v(-89.1, -147.56) * mm, v(-91.14, -145.21) * mm, v(-92.83, -143) * mm, v(-94.14, -140.98) * mm, v(-94.93, -139.51) * mm, v(-95.4, -138.5) * mm, v(-95.62, -137.93) * mm, v(-95.76, -137.52) * mm, v(-95.85, -137.24) * mm, v(-95.93, -136.97) * mm, v(-96.02, -136.62) * mm, v(-96.11, -136.18) * mm, v(-96.23, -135.45) * mm, v(-96.31, -134.46) * mm, v(-96.3, -133.04) * mm, v(-96.14, -131.32) * mm, v(-95.82, -129.29) * mm, v(-95.17, -126.15) * mm, v(-94.2, -122.4) * mm, v(-93.04, -118.06) * mm, v(-92.14, -114.5) * mm, v(-91.26, -110.63) * mm, v(-90.47, -106.44) * mm, v(-89.98, -102.68) * mm, v(-89.72, -99.51) * mm, v(-89.61, -97.06) * mm, v(-89.6, -94.53) * mm, v(-89.7, -91.94) * mm, v(-89.88, -89.73) * mm, v(-90.1, -87.93) * mm, v(-90.35, -86.12) * mm, v(-90.75, -83.9) * mm, v(-91.33, -81.3) * mm, v(-92, -78.76) * mm, v(-93, -75.45) * mm, v(-94.44, -71.44) * mm, v(-96.37, -66.81) * mm, v(-98.47, -62.31) * mm, v(-101.43, -56.47) * mm, v(-105.34, -49.38) * mm, v(-110.1, -41.14) * mm, v(-114.67, -33.14) * mm, v(-118.77, -25.43) * mm, v(-121.62, -19.33) * mm, v(-123.44, -14.7) * mm, v(-124.57, -11.4) * mm, v(-125.44, -8.25) * mm, v(-125.95, -5.8) * mm, v(-126.23, -3.92) * mm, v(-126.37, -2.57) * mm, v(-126.45, -1.48) * mm, v(-126.48, -0.62) * mm, v(-126.48, 0) * mm, v(-126.48, 0.62) * mm]});
            skFitSpline(sketch, "E127.trimOffspring", {"points": [v(-126.48, -0.62) * mm, v(-126.48, 0) * mm, v(-126.48, 0.62) * mm, v(-126.45, 1.48) * mm, v(-126.37, 2.57) * mm, v(-126.23, 3.92) * mm, v(-125.95, 5.8) * mm, v(-125.44, 8.25) * mm, v(-124.57, 11.4) * mm, v(-123.44, 14.7) * mm, v(-121.62, 19.33) * mm, v(-118.77, 25.43) * mm, v(-114.67, 33.14) * mm, v(-110.1, 41.14) * mm, v(-105.34, 49.38) * mm, v(-101.43, 56.47) * mm, v(-98.47, 62.31) * mm, v(-96.37, 66.81) * mm, v(-94.44, 71.44) * mm, v(-93, 75.45) * mm, v(-92, 78.76) * mm, v(-91.33, 81.3) * mm, v(-90.75, 83.9) * mm, v(-90.35, 86.12) * mm, v(-90.1, 87.93) * mm, v(-89.88, 89.73) * mm, v(-89.7, 91.94) * mm, v(-89.6, 94.53) * mm, v(-89.61, 97.06) * mm, v(-89.72, 99.51) * mm, v(-89.98, 102.68) * mm, v(-90.47, 106.44) * mm, v(-91.26, 110.63) * mm, v(-92.14, 114.5) * mm, v(-93.04, 118.06) * mm, v(-94.2, 122.4) * mm, v(-95.17, 126.15) * mm, v(-95.82, 129.29) * mm, v(-96.14, 131.32) * mm, v(-96.3, 133.04) * mm, v(-96.31, 134.46) * mm, v(-96.23, 135.45) * mm, v(-96.11, 136.18) * mm, v(-96.02, 136.62) * mm, v(-95.93, 136.97) * mm, v(-95.85, 137.24) * mm, v(-95.76, 137.52) * mm, v(-95.62, 137.93) * mm, v(-95.4, 138.5) * mm, v(-94.93, 139.51) * mm, v(-94.14, 140.98) * mm, v(-92.83, 143) * mm, v(-91.14, 145.21) * mm, v(-89.1, 147.56) * mm, v(-86.7, 150.02) * mm, v(-83.04, 153.37) * mm, v(-77.67, 157.62) * mm, v(-70.12, 162.62) * mm, v(-61.63, 167.33) * mm, v(-52.35, 171.62) * mm, v(-42.46, 175.35) * mm, v(-32.12, 178.4) * mm, v(-23.26, 180.32) * mm, v(-16.1, 181.41) * mm, v(-10.72, 182.01) * mm, v(-6.24, 182.32) * mm, v(-2.67, 182.44) * mm, v(0, 182.47) * mm, v(2.67, 182.44) * mm, v(6.24, 182.32) * mm, v(10.72, 182.01) * mm, v(16.1, 181.41) * mm, v(23.26, 180.32) * mm, v(32.12, 178.4) * mm, v(42.46, 175.35) * mm, v(52.35, 171.62) * mm, v(61.63, 167.33) * mm, v(70.12, 162.62) * mm, v(77.67, 157.62) * mm, v(83.04, 153.37) * mm, v(86.7, 150.02) * mm, v(89.1, 147.56) * mm, v(91.14, 145.21) * mm, v(92.83, 143) * mm, v(94.14, 140.98) * mm, v(94.93, 139.51) * mm, v(95.4, 138.5) * mm, v(95.62, 137.93) * mm, v(95.76, 137.52) * mm, v(95.85, 137.24) * mm, v(95.93, 136.97) * mm, v(96.02, 136.62) * mm, v(96.11, 136.18) * mm, v(96.23, 135.45) * mm, v(96.31, 134.46) * mm, v(96.3, 133.04) * mm, v(96.14, 131.32) * mm, v(95.82, 129.29) * mm, v(95.17, 126.15) * mm, v(94.2, 122.4) * mm, v(93.04, 118.06) * mm, v(92.14, 114.5) * mm, v(91.26, 110.63) * mm, v(90.47, 106.44) * mm, v(89.98, 102.68) * mm, v(89.72, 99.51) * mm, v(89.61, 97.06) * mm, v(89.6, 94.53) * mm, v(89.7, 91.94) * mm, v(89.88, 89.73) * mm, v(90.1, 87.93) * mm, v(90.35, 86.12) * mm, v(90.75, 83.9) * mm, v(91.33, 81.3) * mm, v(92, 78.76) * mm, v(93, 75.45) * mm, v(94.44, 71.44) * mm, v(96.37, 66.81) * mm, v(98.47, 62.31) * mm, v(101.43, 56.47) * mm, v(105.34, 49.38) * mm, v(110.1, 41.14) * mm, v(114.67, 33.14) * mm, v(118.77, 25.43) * mm, v(121.62, 19.33) * mm, v(123.44, 14.7) * mm, v(124.57, 11.4) * mm, v(125.44, 8.25) * mm, v(125.95, 5.8) * mm, v(126.23, 3.92) * mm, v(126.37, 2.57) * mm, v(126.45, 1.48) * mm, v(126.48, 0.62) * mm, v(126.48, 0) * mm, v(126.48, -0.62) * mm, v(126.45, -1.48) * mm, v(126.37, -2.57) * mm, v(126.23, -3.92) * mm, v(125.95, -5.8) * mm, v(125.44, -8.25) * mm, v(124.57, -11.4) * mm, v(123.44, -14.7) * mm, v(121.62, -19.33) * mm, v(118.77, -25.43) * mm, v(114.67, -33.14) * mm, v(110.1, -41.14) * mm, v(105.34, -49.38) * mm, v(101.43, -56.47) * mm, v(98.47, -62.31) * mm, v(96.37, -66.81) * mm, v(94.44, -71.44) * mm, v(93, -75.45) * mm, v(92, -78.76) * mm, v(91.33, -81.3) * mm, v(90.75, -83.9) * mm, v(90.35, -86.12) * mm, v(90.1, -87.93) * mm, v(89.88, -89.73) * mm, v(89.7, -91.94) * mm, v(89.6, -94.53) * mm, v(89.61, -97.06) * mm, v(89.72, -99.51) * mm, v(89.98, -102.68) * mm, v(90.47, -106.44) * mm, v(91.26, -110.63) * mm, v(92.14, -114.5) * mm, v(93.04, -118.06) * mm, v(94.2, -122.4) * mm, v(95.17, -126.15) * mm, v(95.82, -129.29) * mm, v(96.14, -131.32) * mm, v(96.3, -133.04) * mm, v(96.31, -134.46) * mm, v(96.23, -135.45) * mm, v(96.11, -136.18) * mm, v(96.02, -136.62) * mm, v(95.93, -136.97) * mm, v(95.85, -137.24) * mm, v(95.76, -137.52) * mm, v(95.62, -137.93) * mm, v(95.4, -138.5) * mm, v(94.93, -139.51) * mm, v(94.14, -140.98) * mm, v(92.83, -143) * mm, v(91.14, -145.21) * mm, v(89.1, -147.56) * mm, v(86.7, -150.02) * mm, v(83.04, -153.37) * mm, v(77.67, -157.62) * mm, v(70.12, -162.62) * mm, v(61.63, -167.33) * mm, v(52.35, -171.62) * mm, v(42.46, -175.35) * mm, v(32.12, -178.4) * mm, v(23.26, -180.32) * mm, v(16.1, -181.41) * mm, v(10.72, -182.01) * mm, v(6.24, -182.32) * mm, v(2.67, -182.44) * mm, v(0, -182.47) * mm, v(-2.67, -182.44) * mm, v(-6.24, -182.32) * mm, v(-10.72, -182.01) * mm, v(-16.1, -181.41) * mm, v(-23.26, -180.32) * mm, v(-32.12, -178.4) * mm, v(-42.46, -175.35) * mm, v(-52.35, -171.62) * mm, v(-61.63, -167.33) * mm, v(-70.12, -162.62) * mm, v(-77.67, -157.62) * mm, v(-83.04, -153.37) * mm, v(-86.7, -150.02) * mm, v(-89.1, -147.56) * mm, v(-91.14, -145.21) * mm, v(-92.83, -143) * mm, v(-94.14, -140.98) * mm, v(-94.93, -139.51) * mm, v(-95.4, -138.5) * mm, v(-95.62, -137.93) * mm, v(-95.76, -137.52) * mm, v(-95.85, -137.24) * mm, v(-95.93, -136.97) * mm, v(-96.02, -136.62) * mm, v(-96.11, -136.18) * mm, v(-96.23, -135.45) * mm, v(-96.31, -134.46) * mm, v(-96.3, -133.04) * mm, v(-96.14, -131.32) * mm, v(-95.82, -129.29) * mm, v(-95.17, -126.15) * mm, v(-94.2, -122.4) * mm, v(-93.04, -118.06) * mm, v(-92.14, -114.5) * mm, v(-91.26, -110.63) * mm, v(-90.47, -106.44) * mm, v(-89.98, -102.68) * mm, v(-89.72, -99.51) * mm, v(-89.61, -97.06) * mm, v(-89.6, -94.53) * mm, v(-89.7, -91.94) * mm, v(-89.88, -89.73) * mm, v(-90.1, -87.93) * mm, v(-90.35, -86.12) * mm, v(-90.75, -83.9) * mm, v(-91.33, -81.3) * mm, v(-92, -78.76) * mm, v(-93, -75.45) * mm, v(-94.44, -71.44) * mm, v(-96.37, -66.81) * mm, v(-98.47, -62.31) * mm, v(-101.43, -56.47) * mm, v(-105.34, -49.38) * mm, v(-110.1, -41.14) * mm, v(-114.67, -33.14) * mm, v(-118.77, -25.43) * mm, v(-121.62, -19.33) * mm, v(-123.44, -14.7) * mm, v(-124.57, -11.4) * mm, v(-125.44, -8.25) * mm, v(-125.95, -5.8) * mm, v(-126.23, -3.92) * mm, v(-126.37, -2.57) * mm, v(-126.45, -1.48) * mm, v(-126.48, -0.62) * mm, v(-126.48, 0) * mm, v(-126.48, 0.62) * mm]});
            skLineSegment(sketch, "E128", {"start": v(0, 0) * mm, "end": v(0, 115.42) * mm, "construction": true});
            skCircle(sketch, "E129", {"center": v(0, 0) * mm, "radius": 10 * mm});
            skFitSpline(sketch, "E130.0", {"points": [v(-141.45, -1.94) * mm, v(-141.5, 0) * mm, v(-141.45, 1.94) * mm, v(-141.28, 4.55) * mm, v(-140.85, 7.83) * mm, v(-140.02, 11.82) * mm, v(-138.53, 17.19) * mm, v(-136, 23.98) * mm, v(-132.17, 32.2) * mm, v(-127.77, 40.44) * mm, v(-123.08, 48.65) * mm, v(-118.37, 56.8) * mm, v(-113.92, 64.9) * mm, v(-110.64, 71.57) * mm, v(-108.42, 76.89) * mm, v(-107, 80.87) * mm, v(-106.05, 84.2) * mm, v(-105.46, 86.86) * mm, v(-105.1, 88.86) * mm, v(-104.84, 90.86) * mm, v(-104.62, 93.49) * mm, v(-104.58, 96.7) * mm, v(-104.82, 100.44) * mm, v(-105.45, 105.27) * mm, v(-106.68, 111.01) * mm, v(-108.42, 117.5) * mm, v(-110.02, 123.62) * mm, v(-110.94, 128.46) * mm, v(-111.29, 132.18) * mm, v(-111.33, 134.9) * mm, v(-111.11, 137.6) * mm, v(-110.7, 139.82) * mm, v(-110.2, 141.62) * mm, v(-109.6, 143.44) * mm, v(-108.6, 145.8) * mm, v(-107.01, 148.71) * mm, v(-105.06, 151.7) * mm, v(-102.75, 154.73) * mm, v(-99.2, 158.8) * mm, v(-93.95, 163.87) * mm, v(-86.44, 169.81) * mm, v(-77.88, 175.47) * mm, v(-65.24, 182.48) * mm, v(-51.04, 188.45) * mm, v(-35.84, 192.95) * mm, v(-24.07, 195.49) * mm, v(-14.08, 196.82) * mm, v(-6.04, 197.37) * mm, v(0, 197.51) * mm, v(6.04, 197.37) * mm, v(14.08, 196.82) * mm, v(24.07, 195.49) * mm, v(35.84, 192.95) * mm, v(51.04, 188.45) * mm, v(65.24, 182.48) * mm, v(77.88, 175.47) * mm, v(86.44, 169.81) * mm, v(93.95, 163.87) * mm, v(99.2, 158.8) * mm, v(102.75, 154.73) * mm, v(105.06, 151.7) * mm, v(107.01, 148.71) * mm, v(108.6, 145.8) * mm, v(109.6, 143.44) * mm, v(110.2, 141.62) * mm, v(110.7, 139.82) * mm, v(111.11, 137.6) * mm, v(111.33, 134.9) * mm, v(111.29, 132.18) * mm, v(110.94, 128.46) * mm, v(110.02, 123.62) * mm, v(108.42, 117.5) * mm, v(106.68, 111.01) * mm, v(105.45, 105.27) * mm, v(104.82, 100.44) * mm, v(104.58, 96.7) * mm, v(104.62, 93.49) * mm, v(104.84, 90.86) * mm, v(105.1, 88.86) * mm, v(105.46, 86.86) * mm, v(106.05, 84.2) * mm, v(107, 80.87) * mm, v(108.42, 76.89) * mm, v(110.64, 71.57) * mm, v(113.92, 64.9) * mm, v(118.37, 56.8) * mm, v(123.08, 48.65) * mm, v(127.77, 40.44) * mm, v(132.17, 32.2) * mm, v(136, 23.98) * mm, v(138.53, 17.19) * mm, v(140.02, 11.82) * mm, v(140.85, 7.83) * mm, v(141.28, 4.55) * mm, v(141.45, 1.94) * mm, v(141.5, 0) * mm, v(141.45, -1.94) * mm, v(141.28, -4.55) * mm, v(140.85, -7.83) * mm, v(140.02, -11.82) * mm, v(138.53, -17.19) * mm, v(136, -23.98) * mm, v(132.17, -32.2) * mm, v(127.77, -40.44) * mm, v(123.08, -48.65) * mm, v(118.37, -56.8) * mm, v(113.92, -64.9) * mm, v(110.64, -71.57) * mm, v(108.42, -76.89) * mm, v(107, -80.87) * mm, v(106.05, -84.2) * mm, v(105.46, -86.86) * mm, v(105.1, -88.86) * mm, v(104.84, -90.86) * mm, v(104.62, -93.49) * mm, v(104.58, -96.7) * mm, v(104.82, -100.44) * mm, v(105.45, -105.27) * mm, v(106.68, -111.01) * mm, v(108.42, -117.5) * mm, v(110.02, -123.62) * mm, v(110.94, -128.46) * mm, v(111.29, -132.18) * mm, v(111.33, -134.9) * mm, v(111.11, -137.6) * mm, v(110.7, -139.82) * mm, v(110.2, -141.62) * mm, v(109.6, -143.44) * mm, v(108.6, -145.8) * mm, v(107.01, -148.71) * mm, v(105.06, -151.7) * mm, v(102.75, -154.73) * mm, v(99.2, -158.8) * mm, v(93.95, -163.87) * mm, v(86.44, -169.81) * mm, v(77.88, -175.47) * mm, v(65.24, -182.48) * mm, v(51.04, -188.45) * mm, v(35.84, -192.95) * mm, v(24.07, -195.49) * mm, v(14.08, -196.82) * mm, v(6.04, -197.37) * mm, v(0, -197.51) * mm, v(-6.04, -197.37) * mm, v(-14.08, -196.82) * mm, v(-24.07, -195.49) * mm, v(-35.84, -192.95) * mm, v(-51.04, -188.45) * mm, v(-65.24, -182.48) * mm, v(-77.88, -175.47) * mm, v(-86.44, -169.81) * mm, v(-93.95, -163.87) * mm, v(-99.2, -158.8) * mm, v(-102.75, -154.73) * mm, v(-105.06, -151.7) * mm, v(-107.01, -148.71) * mm, v(-108.6, -145.8) * mm, v(-109.6, -143.44) * mm, v(-110.2, -141.62) * mm, v(-110.7, -139.82) * mm, v(-111.11, -137.6) * mm, v(-111.33, -134.9) * mm, v(-111.29, -132.18) * mm, v(-110.94, -128.46) * mm, v(-110.02, -123.62) * mm, v(-108.42, -117.5) * mm, v(-106.68, -111.01) * mm, v(-105.45, -105.27) * mm, v(-104.82, -100.44) * mm, v(-104.58, -96.7) * mm, v(-104.62, -93.49) * mm, v(-104.84, -90.86) * mm, v(-105.1, -88.86) * mm, v(-105.46, -86.86) * mm, v(-106.05, -84.2) * mm, v(-107, -80.87) * mm, v(-108.42, -76.89) * mm, v(-110.64, -71.57) * mm, v(-113.92, -64.9) * mm, v(-118.37, -56.8) * mm, v(-123.08, -48.65) * mm, v(-127.77, -40.44) * mm, v(-132.17, -32.2) * mm, v(-136, -23.98) * mm, v(-138.53, -17.19) * mm, v(-140.02, -11.82) * mm, v(-140.85, -7.83) * mm, v(-141.28, -4.55) * mm, v(-141.45, -1.94) * mm, v(-141.5, 0) * mm, v(-141.45, 1.94) * mm]});
            skArc(sketch, "E131", {"start": v(-90.8, 108.11) * mm, "mid": v(-91.7, 77.84) * mm, "end": v(-104.74, 50.51) * mm});
            skPoint(sketch, "E132.end.orphan", {"position": v(-63.23, 78.19) * mm});
            skPoint(sketch, "E133.center.orphan", {"position": v(-93.23, 78.21) * mm});
            skPoint(sketch, "E133.end.orphan", {"position": v(-77.84, 52.46) * mm});
            skFitSpline(sketch, "E134.trimOffspring", {"points": [v(-141.45, -1.94) * mm, v(-141.5, 0) * mm, v(-141.45, 1.94) * mm, v(-141.28, 4.55) * mm, v(-140.85, 7.83) * mm, v(-140.02, 11.82) * mm, v(-138.53, 17.19) * mm, v(-136, 23.98) * mm, v(-132.17, 32.2) * mm, v(-127.77, 40.44) * mm, v(-123.08, 48.65) * mm, v(-118.37, 56.8) * mm, v(-113.92, 64.9) * mm, v(-110.64, 71.57) * mm, v(-108.42, 76.89) * mm, v(-107, 80.87) * mm, v(-106.05, 84.2) * mm, v(-105.46, 86.86) * mm, v(-105.1, 88.86) * mm, v(-104.84, 90.86) * mm, v(-104.62, 93.49) * mm, v(-104.58, 96.7) * mm, v(-104.82, 100.44) * mm, v(-105.45, 105.27) * mm, v(-106.68, 111.01) * mm, v(-108.42, 117.5) * mm, v(-110.02, 123.62) * mm, v(-110.94, 128.46) * mm, v(-111.29, 132.18) * mm, v(-111.33, 134.9) * mm, v(-111.11, 137.6) * mm, v(-110.7, 139.82) * mm, v(-110.2, 141.62) * mm, v(-109.6, 143.44) * mm, v(-108.6, 145.8) * mm, v(-107.01, 148.71) * mm, v(-105.06, 151.7) * mm, v(-102.75, 154.73) * mm, v(-99.2, 158.8) * mm, v(-93.95, 163.87) * mm, v(-86.44, 169.81) * mm, v(-77.88, 175.47) * mm, v(-65.24, 182.48) * mm, v(-51.04, 188.45) * mm, v(-35.84, 192.95) * mm, v(-24.07, 195.49) * mm, v(-14.08, 196.82) * mm, v(-6.04, 197.37) * mm, v(0, 197.51) * mm, v(6.04, 197.37) * mm, v(14.08, 196.82) * mm, v(24.07, 195.49) * mm, v(35.84, 192.95) * mm, v(51.04, 188.45) * mm, v(65.24, 182.48) * mm, v(77.88, 175.47) * mm, v(86.44, 169.81) * mm, v(93.95, 163.87) * mm, v(99.2, 158.8) * mm, v(102.75, 154.73) * mm, v(105.06, 151.7) * mm, v(107.01, 148.71) * mm, v(108.6, 145.8) * mm, v(109.6, 143.44) * mm, v(110.2, 141.62) * mm, v(110.7, 139.82) * mm, v(111.11, 137.6) * mm, v(111.33, 134.9) * mm, v(111.29, 132.18) * mm, v(110.94, 128.46) * mm, v(110.02, 123.62) * mm, v(108.42, 117.5) * mm, v(106.68, 111.01) * mm, v(105.45, 105.27) * mm, v(104.82, 100.44) * mm, v(104.58, 96.7) * mm, v(104.62, 93.49) * mm, v(104.84, 90.86) * mm, v(105.1, 88.86) * mm, v(105.46, 86.86) * mm, v(106.05, 84.2) * mm, v(107, 80.87) * mm, v(108.42, 76.89) * mm, v(110.64, 71.57) * mm, v(113.92, 64.9) * mm, v(118.37, 56.8) * mm, v(123.08, 48.65) * mm, v(127.77, 40.44) * mm, v(132.17, 32.2) * mm, v(136, 23.98) * mm, v(138.53, 17.19) * mm, v(140.02, 11.82) * mm, v(140.85, 7.83) * mm, v(141.28, 4.55) * mm, v(141.45, 1.94) * mm, v(141.5, 0) * mm, v(141.45, -1.94) * mm, v(141.28, -4.55) * mm, v(140.85, -7.83) * mm, v(140.02, -11.82) * mm, v(138.53, -17.19) * mm, v(136, -23.98) * mm, v(132.17, -32.2) * mm, v(127.77, -40.44) * mm, v(123.08, -48.65) * mm, v(118.37, -56.8) * mm, v(113.92, -64.9) * mm, v(110.64, -71.57) * mm, v(108.42, -76.89) * mm, v(107, -80.87) * mm, v(106.05, -84.2) * mm, v(105.46, -86.86) * mm, v(105.1, -88.86) * mm, v(104.84, -90.86) * mm, v(104.62, -93.49) * mm, v(104.58, -96.7) * mm, v(104.82, -100.44) * mm, v(105.45, -105.27) * mm, v(106.68, -111.01) * mm, v(108.42, -117.5) * mm, v(110.02, -123.62) * mm, v(110.94, -128.46) * mm, v(111.29, -132.18) * mm, v(111.33, -134.9) * mm, v(111.11, -137.6) * mm, v(110.7, -139.82) * mm, v(110.2, -141.62) * mm, v(109.6, -143.44) * mm, v(108.6, -145.8) * mm, v(107.01, -148.71) * mm, v(105.06, -151.7) * mm, v(102.75, -154.73) * mm, v(99.2, -158.8) * mm, v(93.95, -163.87) * mm, v(86.44, -169.81) * mm, v(77.88, -175.47) * mm, v(65.24, -182.48) * mm, v(51.04, -188.45) * mm, v(35.84, -192.95) * mm, v(24.07, -195.49) * mm, v(14.08, -196.82) * mm, v(6.04, -197.37) * mm, v(0, -197.51) * mm, v(-6.04, -197.37) * mm, v(-14.08, -196.82) * mm, v(-24.07, -195.49) * mm, v(-35.84, -192.95) * mm, v(-51.04, -188.45) * mm, v(-65.24, -182.48) * mm, v(-77.88, -175.47) * mm, v(-86.44, -169.81) * mm, v(-93.95, -163.87) * mm, v(-99.2, -158.8) * mm, v(-102.75, -154.73) * mm, v(-105.06, -151.7) * mm, v(-107.01, -148.71) * mm, v(-108.6, -145.8) * mm, v(-109.6, -143.44) * mm, v(-110.2, -141.62) * mm, v(-110.7, -139.82) * mm, v(-111.11, -137.6) * mm, v(-111.33, -134.9) * mm, v(-111.29, -132.18) * mm, v(-110.94, -128.46) * mm, v(-110.02, -123.62) * mm, v(-108.42, -117.5) * mm, v(-106.68, -111.01) * mm, v(-105.45, -105.27) * mm, v(-104.82, -100.44) * mm, v(-104.58, -96.7) * mm, v(-104.62, -93.49) * mm, v(-104.84, -90.86) * mm, v(-105.1, -88.86) * mm, v(-105.46, -86.86) * mm, v(-106.05, -84.2) * mm, v(-107, -80.87) * mm, v(-108.42, -76.89) * mm, v(-110.64, -71.57) * mm, v(-113.92, -64.9) * mm, v(-118.37, -56.8) * mm, v(-123.08, -48.65) * mm, v(-127.77, -40.44) * mm, v(-132.17, -32.2) * mm, v(-136, -23.98) * mm, v(-138.53, -17.19) * mm, v(-140.02, -11.82) * mm, v(-140.85, -7.83) * mm, v(-141.28, -4.55) * mm, v(-141.45, -1.94) * mm, v(-141.5, 0) * mm, v(-141.45, 1.94) * mm]});
            skPoint(sketch, "E135.MirrorCS.end.orphan", {"position": v(-63.23, -78.19) * mm});
            skPoint(sketch, "E136.orphan", {"position": v(-77.84, -52.46) * mm});
            skPoint(sketch, "E137.MirrorCS.end.orphan", {"position": v(63.23, -78.19) * mm});
            skPoint(sketch, "E138.MirrorCS.start.orphan", {"position": v(104.74, 50.51) * mm});
            skPoint(sketch, "E139.trimOffspring.end.orphan", {"position": v(90.8, 108.11) * mm});
            skPoint(sketch, "E140.MirrorCS.end.orphan", {"position": v(63.23, 78.19) * mm});
            skPoint(sketch, "E140.MirrorCS.start.orphan", {"position": v(77.84, 52.46) * mm});
            skArc(sketch, "E141", {"start": v(-90.8, -108.11) * mm, "mid": v(-91.7, -77.84) * mm, "end": v(-104.74, -50.51) * mm});
            skArc(sketch, "E142", {"start": v(90.8, -108.11) * mm, "mid": v(91.7, -77.84) * mm, "end": v(104.74, -50.51) * mm});
            skPoint(sketch, "E143.MirrorCS.end.orphan", {"position": v(77.84, -52.46) * mm});
            skCircle(sketch, "E144", {"center": v(-125.8, 203.68) * mm, "radius": 5 * mm});
            skLineSegment(sketch, "E145", {"start": v(-327.56, 0) * mm, "end": v(211.82, 0) * mm, "construction": true});
            skLineSegment(sketch, "E146", {"start": v(0, 135.6) * mm, "end": v(0, -42.3) * mm, "construction": true});
            const initialGuessF1  = {"E96.0": [0, 0.08288104439999998, 1, 0, 0.13267715999999996, 0.11958350000000001, 0, 0.055173648266843435], "E97.MirrorC": [0, -0.08288104439999998, 1, 0, 0.13267715999999996, 0.11958350000000001, 3.141592653589793, 3.1966594490639286], "E113.trimOffspring": [0, -0.08288104439999998, 1, 0, 0.13267715999999996, 0.11958350000000001, 4.382070923725125, 5.042707037044202], "E114.trimOffspring": [0, 0.08288104439999998, 1, 0, 0.13267715999999996, 0.11958350000000001, 1.2404782701353567, 1.9011143834544768], "E115.trimOffspring": [0, 0.08288104439999998, 1, 0, 0.13267715999999996, 0.11958350000000001, 3.0865258581156554, 3.141592653589793], "E116.trimOffspring": [0, -0.08288104439999998, 1, 0, 0.13267715999999996, 0.11958350000000001, 6.228011658912739, 0]};
            skSetInitialGuess(sketch, initialGuessF1);
            skSolve(sketch);
        }
        {
            var Q0;
            {var subQ0=sQuery(id+"F1.wireOp",EDGE,"E113.trimOffspring");var subQ1=sQuery(id+"F1.wireOp",EDGE,"E109");var subQ8=makeQuery(id+"F1.imprint","INTERSECT",VERTEX,{"disambiguationData":[OD(1.0)],"derivedFrom":[subQ1,subQ0]});Q0=makeQuery(id+"F1.imprint","IMPRINT",FACE,{"disambiguationData":[TD([[makeQuery(id+"F1.imprint","IMPRINT",EDGE,{"disambiguationData":[TD([[subQ8,-1.0]])],"derivedFrom":subQ1}),-1.0]])]});}
            var Q1;
            {var subQ0=sQuery(id+"F1.wireOp",EDGE,"E114.trimOffspring");var subQ1=sQuery(id+"F1.wireOp",EDGE,"E109");var subQ6=makeQuery(id+"F1.imprint","INTERSECT",VERTEX,{"derivedFrom":[subQ1,subQ0]});Q1=makeQuery(id+"F1.imprint","IMPRINT",FACE,{"disambiguationData":[TD([[makeQuery(id+"F1.imprint","IMPRINT",EDGE,{"disambiguationData":[TD([[subQ6,1.0]])],"derivedFrom":subQ1}),-1.0]])]});}
            extrude(context, id + "F2", {"entities" : qUnion([Q0, Q1]), "depth" : 20 * mm, "offsetDistance" : 25 * mm});
        }
        {
            var Q0;
            Q0=makeQuery(id+"F2.opExtrude","CAP_FACE",FACE,{"disambiguationData":[OSD([sQuery(id+"F0.wireOp",EDGE,"E90"),sQuery(id+"F1.wireOp",EDGE,"E109"),sQuery(id+"F1.wireOp",EDGE,"E117"),sQuery(id+"F1.wireOp",EDGE,"E119.MirrorC"),sQuery(id+"F1.wireOp",EDGE,"E121"),sQuery(id+"F1.wireOp",EDGE,"E133"),sQuery(id+"F1.wireOp",EDGE,"E122.0"),sQuery(id+"F1.wireOp",EDGE,"4ed58db8-271b-406d-964a-2f730ead86820.MirrorCS"),sQuery(id+"F1.wireOp",EDGE,"E123.MirrorC"),sQuery(id+"F1.wireOp",EDGE,"E143.MirrorCS"),sQuery(id+"F1.wireOp",EDGE,"E124.MirrorC"),sQuery(id+"F1.wireOp",EDGE,"E138.MirrorCS"),sQuery(id+"F1.wireOp",EDGE,"E125.MirrorC"),sQuery(id+"F1.wireOp",EDGE,"E126.trimOffspring"),sQuery(id+"F1.wireOp",EDGE,"E127.trimOffspring"),sQuery(id+"F1.wireOp",EDGE,"E132"),sQuery(id+"F1.wireOp",EDGE,"336bbe1f-9501-4eec-9308-17306a1db98d.trimOffspring"),sQuery(id+"F1.wireOp",EDGE,"E135.MirrorCS"),sQuery(id+"F1.wireOp",EDGE,"E140.MirrorCS"),sQuery(id+"F1.wireOp",EDGE,"E137.MirrorCS"),sQuery(id+"F1.wireOp",EDGE,"E139.trimOffspring"),sQuery(id+"F1.wireOp",EDGE,"137d6f6d-0ba0-48c0-837d-3dac90d6f9ea.trimOffspring"),sQuery(id+"F1.wireOp",EDGE,"81168a5f-c75b-4f20-9658-c9bd9ac01868.trimOffspring")])],"isStart":false});
            cPlane(context, id + "F3", {"entities" : qUnion([Q0]), "cplaneType" : CPlaneType.OFFSET, "offset" : 50 * mm, "width" : 150 * mm, "height" : 150 * mm});
        }
        {
            var Q0;
            Q0=qCreatedBy(id+"F3.planeOp",FACE);
            var sketch = newSketch(context, id + "F4", { "sketchPlane" : qUnion([Q0])});
            skFitSpline(sketch, "E147.0.0", {"points": [v(-146.48, 0) * mm, v(-146.48, -31.99) * mm, v(-89.5, -87.65) * mm, v(-140.83, -150.23) * mm, v(0, -234.29) * mm, v(140.83, -150.23) * mm, v(89.5, -87.65) * mm, v(179.22, 0) * mm, v(89.5, 87.65) * mm, v(140.83, 150.23) * mm, v(0, 234.29) * mm, v(-140.83, 150.23) * mm, v(-89.5, 87.65) * mm, v(-146.48, 31.99) * mm, v(-146.48, 0) * mm]});
            skEllipticalArc(sketch, "E147.0.1", {});
            skFitSpline(sketch, "E147.0.2", {"points": [v(-146.48, 0) * mm, v(-146.48, -31.99) * mm, v(-89.5, -87.65) * mm, v(-140.83, -150.23) * mm, v(0, -234.29) * mm, v(140.83, -150.23) * mm, v(89.5, -87.65) * mm, v(179.22, 0) * mm, v(89.5, 87.65) * mm, v(140.83, 150.23) * mm, v(0, 234.29) * mm, v(-140.83, 150.23) * mm, v(-89.5, 87.65) * mm, v(-146.48, 31.99) * mm, v(-146.48, 0) * mm]});
            skEllipticalArc(sketch, "E147.0.3", {});
            skArc(sketch, "E148.0", {"start": v(-90.8, -108.11) * mm, "mid": v(-91.7, -77.84) * mm, "end": v(-104.74, -50.51) * mm});
            skFitSpline(sketch, "E149.0", {"points": [v(-126.48, 0) * mm, v(-126.48, 0.2) * mm, v(-126.48, 0.62) * mm, v(-126.45, 1.48) * mm, v(-126.37, 2.57) * mm, v(-126.23, 3.92) * mm, v(-125.95, 5.8) * mm, v(-125.44, 8.25) * mm, v(-124.57, 11.4) * mm, v(-123.44, 14.7) * mm, v(-121.62, 19.33) * mm, v(-118.77, 25.43) * mm, v(-114.67, 33.14) * mm, v(-110.1, 41.14) * mm, v(-105.34, 49.38) * mm, v(-101.43, 56.47) * mm, v(-98.47, 62.31) * mm, v(-96.37, 66.81) * mm, v(-94.44, 71.44) * mm, v(-93, 75.45) * mm, v(-92, 78.76) * mm, v(-91.33, 81.3) * mm, v(-90.75, 83.9) * mm, v(-90.35, 86.12) * mm, v(-90.1, 87.93) * mm, v(-89.88, 89.73) * mm, v(-89.7, 91.94) * mm, v(-89.6, 94.53) * mm, v(-89.61, 97.06) * mm, v(-89.72, 99.51) * mm, v(-89.98, 102.68) * mm, v(-90.47, 106.44) * mm, v(-91.26, 110.63) * mm, v(-92.14, 114.5) * mm, v(-93.04, 118.06) * mm, v(-94.2, 122.4) * mm, v(-95.17, 126.15) * mm, v(-95.82, 129.29) * mm, v(-96.14, 131.32) * mm, v(-96.3, 133.04) * mm, v(-96.31, 134.46) * mm, v(-96.23, 135.45) * mm, v(-96.11, 136.18) * mm, v(-96.02, 136.62) * mm, v(-95.93, 136.97) * mm, v(-95.85, 137.24) * mm, v(-95.76, 137.52) * mm, v(-95.62, 137.93) * mm, v(-95.4, 138.5) * mm, v(-94.93, 139.51) * mm, v(-94.14, 140.98) * mm, v(-92.83, 143) * mm, v(-91.14, 145.21) * mm, v(-89.1, 147.56) * mm, v(-86.7, 150.02) * mm, v(-83.04, 153.37) * mm, v(-77.67, 157.62) * mm, v(-70.12, 162.62) * mm, v(-61.63, 167.33) * mm, v(-52.35, 171.62) * mm, v(-42.46, 175.35) * mm, v(-32.12, 178.4) * mm, v(-23.26, 180.32) * mm, v(-16.1, 181.41) * mm, v(-10.72, 182.01) * mm, v(-6.24, 182.32) * mm, v(-2.67, 182.44) * mm, v(0, 182.47) * mm, v(2.67, 182.44) * mm, v(6.24, 182.32) * mm, v(10.72, 182.01) * mm, v(16.1, 181.41) * mm, v(23.26, 180.32) * mm, v(32.12, 178.4) * mm, v(42.46, 175.35) * mm, v(52.35, 171.62) * mm, v(61.63, 167.33) * mm, v(70.12, 162.62) * mm, v(77.67, 157.62) * mm, v(83.04, 153.37) * mm, v(86.7, 150.02) * mm, v(89.1, 147.56) * mm, v(91.14, 145.21) * mm, v(92.83, 143) * mm, v(94.14, 140.98) * mm, v(94.93, 139.51) * mm, v(95.4, 138.5) * mm, v(95.62, 137.93) * mm, v(95.76, 137.52) * mm, v(95.85, 137.24) * mm, v(95.93, 136.97) * mm, v(96.02, 136.62) * mm, v(96.11, 136.18) * mm, v(96.23, 135.45) * mm, v(96.31, 134.46) * mm, v(96.3, 133.04) * mm, v(96.14, 131.32) * mm, v(95.82, 129.29) * mm, v(95.17, 126.15) * mm, v(94.2, 122.4) * mm, v(93.04, 118.06) * mm, v(92.14, 114.5) * mm, v(91.26, 110.63) * mm, v(90.47, 106.44) * mm, v(89.98, 102.68) * mm, v(89.72, 99.51) * mm, v(89.61, 97.06) * mm, v(89.6, 94.53) * mm, v(89.7, 91.94) * mm, v(89.88, 89.73) * mm, v(90.1, 87.93) * mm, v(90.35, 86.12) * mm, v(90.75, 83.9) * mm, v(91.33, 81.3) * mm, v(92, 78.76) * mm, v(93, 75.45) * mm, v(94.44, 71.44) * mm, v(96.37, 66.81) * mm, v(98.47, 62.31) * mm, v(101.43, 56.47) * mm, v(105.34, 49.38) * mm, v(110.1, 41.14) * mm, v(114.67, 33.14) * mm, v(118.77, 25.43) * mm, v(121.62, 19.33) * mm, v(123.44, 14.7) * mm, v(124.57, 11.4) * mm, v(125.44, 8.25) * mm, v(125.95, 5.8) * mm, v(126.23, 3.92) * mm, v(126.37, 2.57) * mm, v(126.45, 1.48) * mm, v(126.48, 0.62) * mm, v(126.48, 0) * mm, v(126.48, -0.62) * mm, v(126.45, -1.48) * mm, v(126.37, -2.57) * mm, v(126.23, -3.92) * mm, v(125.95, -5.8) * mm, v(125.44, -8.25) * mm, v(124.57, -11.4) * mm, v(123.44, -14.7) * mm, v(121.62, -19.33) * mm, v(118.77, -25.43) * mm, v(114.67, -33.14) * mm, v(110.1, -41.14) * mm, v(105.34, -49.38) * mm, v(101.43, -56.47) * mm, v(98.47, -62.31) * mm, v(96.37, -66.81) * mm, v(94.44, -71.44) * mm, v(93, -75.45) * mm, v(92, -78.76) * mm, v(91.33, -81.3) * mm, v(90.75, -83.9) * mm, v(90.35, -86.12) * mm, v(90.1, -87.93) * mm, v(89.88, -89.73) * mm, v(89.7, -91.94) * mm, v(89.6, -94.53) * mm, v(89.61, -97.06) * mm, v(89.72, -99.51) * mm, v(89.98, -102.68) * mm, v(90.47, -106.44) * mm, v(91.26, -110.63) * mm, v(92.14, -114.5) * mm, v(93.04, -118.06) * mm, v(94.2, -122.4) * mm, v(95.17, -126.15) * mm, v(95.82, -129.29) * mm, v(96.14, -131.32) * mm, v(96.3, -133.04) * mm, v(96.31, -134.46) * mm, v(96.23, -135.45) * mm, v(96.11, -136.18) * mm, v(96.02, -136.62) * mm, v(95.93, -136.97) * mm, v(95.85, -137.24) * mm, v(95.76, -137.52) * mm, v(95.62, -137.93) * mm, v(95.4, -138.5) * mm, v(94.93, -139.51) * mm, v(94.14, -140.98) * mm, v(92.83, -143) * mm, v(91.14, -145.21) * mm, v(89.1, -147.56) * mm, v(86.7, -150.02) * mm, v(83.04, -153.37) * mm, v(77.67, -157.62) * mm, v(70.12, -162.62) * mm, v(61.63, -167.33) * mm, v(52.35, -171.62) * mm, v(42.46, -175.35) * mm, v(32.12, -178.4) * mm, v(23.26, -180.32) * mm, v(16.1, -181.41) * mm, v(10.72, -182.01) * mm, v(6.24, -182.32) * mm, v(2.67, -182.44) * mm, v(0, -182.47) * mm, v(-2.67, -182.44) * mm, v(-6.24, -182.32) * mm, v(-10.72, -182.01) * mm, v(-16.1, -181.41) * mm, v(-23.26, -180.32) * mm, v(-32.12, -178.4) * mm, v(-42.46, -175.35) * mm, v(-52.35, -171.62) * mm, v(-61.63, -167.33) * mm, v(-70.12, -162.62) * mm, v(-77.67, -157.62) * mm, v(-83.04, -153.37) * mm, v(-86.7, -150.02) * mm, v(-89.1, -147.56) * mm, v(-91.14, -145.21) * mm, v(-92.83, -143) * mm, v(-94.14, -140.98) * mm, v(-94.93, -139.51) * mm, v(-95.4, -138.5) * mm, v(-95.62, -137.93) * mm, v(-95.76, -137.52) * mm, v(-95.85, -137.24) * mm, v(-95.93, -136.97) * mm, v(-96.02, -136.62) * mm, v(-96.11, -136.18) * mm, v(-96.23, -135.45) * mm, v(-96.31, -134.46) * mm, v(-96.3, -133.04) * mm, v(-96.14, -131.32) * mm, v(-95.82, -129.29) * mm, v(-95.17, -126.15) * mm, v(-94.2, -122.4) * mm, v(-93.04, -118.06) * mm, v(-92.14, -114.5) * mm, v(-91.26, -110.63) * mm, v(-90.47, -106.44) * mm, v(-89.98, -102.68) * mm, v(-89.72, -99.51) * mm, v(-89.61, -97.06) * mm, v(-89.6, -94.53) * mm, v(-89.7, -91.94) * mm, v(-89.88, -89.73) * mm, v(-90.1, -87.93) * mm, v(-90.35, -86.12) * mm, v(-90.75, -83.9) * mm, v(-91.33, -81.3) * mm, v(-92, -78.76) * mm, v(-93, -75.45) * mm, v(-94.44, -71.44) * mm, v(-96.37, -66.81) * mm, v(-98.47, -62.31) * mm, v(-101.43, -56.47) * mm, v(-105.34, -49.38) * mm, v(-110.1, -41.14) * mm, v(-114.67, -33.14) * mm, v(-118.77, -25.43) * mm, v(-121.62, -19.33) * mm, v(-123.44, -14.7) * mm, v(-124.57, -11.4) * mm, v(-125.44, -8.25) * mm, v(-125.95, -5.8) * mm, v(-126.23, -3.92) * mm, v(-126.37, -2.57) * mm, v(-126.45, -1.48) * mm, v(-126.48, -0.62) * mm, v(-126.48, -0.2) * mm, v(-126.48, 0) * mm]});
            skArc(sketch, "E150.0", {"start": v(90.8, -108.11) * mm, "mid": v(91.7, -77.84) * mm, "end": v(104.74, -50.51) * mm});
            skFitSpline(sketch, "E151.0", {"points": [v(-126.48, 0) * mm, v(-126.48, 0.2) * mm, v(-126.48, 0.62) * mm, v(-126.45, 1.48) * mm, v(-126.37, 2.57) * mm, v(-126.23, 3.92) * mm, v(-125.95, 5.8) * mm, v(-125.44, 8.25) * mm, v(-124.57, 11.4) * mm, v(-123.44, 14.7) * mm, v(-121.62, 19.33) * mm, v(-118.77, 25.43) * mm, v(-114.67, 33.14) * mm, v(-110.1, 41.14) * mm, v(-105.34, 49.38) * mm, v(-101.43, 56.47) * mm, v(-98.47, 62.31) * mm, v(-96.37, 66.81) * mm, v(-94.44, 71.44) * mm, v(-93, 75.45) * mm, v(-92, 78.76) * mm, v(-91.33, 81.3) * mm, v(-90.75, 83.9) * mm, v(-90.35, 86.12) * mm, v(-90.1, 87.93) * mm, v(-89.88, 89.73) * mm, v(-89.7, 91.94) * mm, v(-89.6, 94.53) * mm, v(-89.61, 97.06) * mm, v(-89.72, 99.51) * mm, v(-89.98, 102.68) * mm, v(-90.47, 106.44) * mm, v(-91.26, 110.63) * mm, v(-92.14, 114.5) * mm, v(-93.04, 118.06) * mm, v(-94.2, 122.4) * mm, v(-95.17, 126.15) * mm, v(-95.82, 129.29) * mm, v(-96.14, 131.32) * mm, v(-96.3, 133.04) * mm, v(-96.31, 134.46) * mm, v(-96.23, 135.45) * mm, v(-96.11, 136.18) * mm, v(-96.02, 136.62) * mm, v(-95.93, 136.97) * mm, v(-95.85, 137.24) * mm, v(-95.76, 137.52) * mm, v(-95.62, 137.93) * mm, v(-95.4, 138.5) * mm, v(-94.93, 139.51) * mm, v(-94.14, 140.98) * mm, v(-92.83, 143) * mm, v(-91.14, 145.21) * mm, v(-89.1, 147.56) * mm, v(-86.7, 150.02) * mm, v(-83.04, 153.37) * mm, v(-77.67, 157.62) * mm, v(-70.12, 162.62) * mm, v(-61.63, 167.33) * mm, v(-52.35, 171.62) * mm, v(-42.46, 175.35) * mm, v(-32.12, 178.4) * mm, v(-23.26, 180.32) * mm, v(-16.1, 181.41) * mm, v(-10.72, 182.01) * mm, v(-6.24, 182.32) * mm, v(-2.67, 182.44) * mm, v(0, 182.47) * mm, v(2.67, 182.44) * mm, v(6.24, 182.32) * mm, v(10.72, 182.01) * mm, v(16.1, 181.41) * mm, v(23.26, 180.32) * mm, v(32.12, 178.4) * mm, v(42.46, 175.35) * mm, v(52.35, 171.62) * mm, v(61.63, 167.33) * mm, v(70.12, 162.62) * mm, v(77.67, 157.62) * mm, v(83.04, 153.37) * mm, v(86.7, 150.02) * mm, v(89.1, 147.56) * mm, v(91.14, 145.21) * mm, v(92.83, 143) * mm, v(94.14, 140.98) * mm, v(94.93, 139.51) * mm, v(95.4, 138.5) * mm, v(95.62, 137.93) * mm, v(95.76, 137.52) * mm, v(95.85, 137.24) * mm, v(95.93, 136.97) * mm, v(96.02, 136.62) * mm, v(96.11, 136.18) * mm, v(96.23, 135.45) * mm, v(96.31, 134.46) * mm, v(96.3, 133.04) * mm, v(96.14, 131.32) * mm, v(95.82, 129.29) * mm, v(95.17, 126.15) * mm, v(94.2, 122.4) * mm, v(93.04, 118.06) * mm, v(92.14, 114.5) * mm, v(91.26, 110.63) * mm, v(90.47, 106.44) * mm, v(89.98, 102.68) * mm, v(89.72, 99.51) * mm, v(89.61, 97.06) * mm, v(89.6, 94.53) * mm, v(89.7, 91.94) * mm, v(89.88, 89.73) * mm, v(90.1, 87.93) * mm, v(90.35, 86.12) * mm, v(90.75, 83.9) * mm, v(91.33, 81.3) * mm, v(92, 78.76) * mm, v(93, 75.45) * mm, v(94.44, 71.44) * mm, v(96.37, 66.81) * mm, v(98.47, 62.31) * mm, v(101.43, 56.47) * mm, v(105.34, 49.38) * mm, v(110.1, 41.14) * mm, v(114.67, 33.14) * mm, v(118.77, 25.43) * mm, v(121.62, 19.33) * mm, v(123.44, 14.7) * mm, v(124.57, 11.4) * mm, v(125.44, 8.25) * mm, v(125.95, 5.8) * mm, v(126.23, 3.92) * mm, v(126.37, 2.57) * mm, v(126.45, 1.48) * mm, v(126.48, 0.62) * mm, v(126.48, 0) * mm, v(126.48, -0.62) * mm, v(126.45, -1.48) * mm, v(126.37, -2.57) * mm, v(126.23, -3.92) * mm, v(125.95, -5.8) * mm, v(125.44, -8.25) * mm, v(124.57, -11.4) * mm, v(123.44, -14.7) * mm, v(121.62, -19.33) * mm, v(118.77, -25.43) * mm, v(114.67, -33.14) * mm, v(110.1, -41.14) * mm, v(105.34, -49.38) * mm, v(101.43, -56.47) * mm, v(98.47, -62.31) * mm, v(96.37, -66.81) * mm, v(94.44, -71.44) * mm, v(93, -75.45) * mm, v(92, -78.76) * mm, v(91.33, -81.3) * mm, v(90.75, -83.9) * mm, v(90.35, -86.12) * mm, v(90.1, -87.93) * mm, v(89.88, -89.73) * mm, v(89.7, -91.94) * mm, v(89.6, -94.53) * mm, v(89.61, -97.06) * mm, v(89.72, -99.51) * mm, v(89.98, -102.68) * mm, v(90.47, -106.44) * mm, v(91.26, -110.63) * mm, v(92.14, -114.5) * mm, v(93.04, -118.06) * mm, v(94.2, -122.4) * mm, v(95.17, -126.15) * mm, v(95.82, -129.29) * mm, v(96.14, -131.32) * mm, v(96.3, -133.04) * mm, v(96.31, -134.46) * mm, v(96.23, -135.45) * mm, v(96.11, -136.18) * mm, v(96.02, -136.62) * mm, v(95.93, -136.97) * mm, v(95.85, -137.24) * mm, v(95.76, -137.52) * mm, v(95.62, -137.93) * mm, v(95.4, -138.5) * mm, v(94.93, -139.51) * mm, v(94.14, -140.98) * mm, v(92.83, -143) * mm, v(91.14, -145.21) * mm, v(89.1, -147.56) * mm, v(86.7, -150.02) * mm, v(83.04, -153.37) * mm, v(77.67, -157.62) * mm, v(70.12, -162.62) * mm, v(61.63, -167.33) * mm, v(52.35, -171.62) * mm, v(42.46, -175.35) * mm, v(32.12, -178.4) * mm, v(23.26, -180.32) * mm, v(16.1, -181.41) * mm, v(10.72, -182.01) * mm, v(6.24, -182.32) * mm, v(2.67, -182.44) * mm, v(0, -182.47) * mm, v(-2.67, -182.44) * mm, v(-6.24, -182.32) * mm, v(-10.72, -182.01) * mm, v(-16.1, -181.41) * mm, v(-23.26, -180.32) * mm, v(-32.12, -178.4) * mm, v(-42.46, -175.35) * mm, v(-52.35, -171.62) * mm, v(-61.63, -167.33) * mm, v(-70.12, -162.62) * mm, v(-77.67, -157.62) * mm, v(-83.04, -153.37) * mm, v(-86.7, -150.02) * mm, v(-89.1, -147.56) * mm, v(-91.14, -145.21) * mm, v(-92.83, -143) * mm, v(-94.14, -140.98) * mm, v(-94.93, -139.51) * mm, v(-95.4, -138.5) * mm, v(-95.62, -137.93) * mm, v(-95.76, -137.52) * mm, v(-95.85, -137.24) * mm, v(-95.93, -136.97) * mm, v(-96.02, -136.62) * mm, v(-96.11, -136.18) * mm, v(-96.23, -135.45) * mm, v(-96.31, -134.46) * mm, v(-96.3, -133.04) * mm, v(-96.14, -131.32) * mm, v(-95.82, -129.29) * mm, v(-95.17, -126.15) * mm, v(-94.2, -122.4) * mm, v(-93.04, -118.06) * mm, v(-92.14, -114.5) * mm, v(-91.26, -110.63) * mm, v(-90.47, -106.44) * mm, v(-89.98, -102.68) * mm, v(-89.72, -99.51) * mm, v(-89.61, -97.06) * mm, v(-89.6, -94.53) * mm, v(-89.7, -91.94) * mm, v(-89.88, -89.73) * mm, v(-90.1, -87.93) * mm, v(-90.35, -86.12) * mm, v(-90.75, -83.9) * mm, v(-91.33, -81.3) * mm, v(-92, -78.76) * mm, v(-93, -75.45) * mm, v(-94.44, -71.44) * mm, v(-96.37, -66.81) * mm, v(-98.47, -62.31) * mm, v(-101.43, -56.47) * mm, v(-105.34, -49.38) * mm, v(-110.1, -41.14) * mm, v(-114.67, -33.14) * mm, v(-118.77, -25.43) * mm, v(-121.62, -19.33) * mm, v(-123.44, -14.7) * mm, v(-124.57, -11.4) * mm, v(-125.44, -8.25) * mm, v(-125.95, -5.8) * mm, v(-126.23, -3.92) * mm, v(-126.37, -2.57) * mm, v(-126.45, -1.48) * mm, v(-126.48, -0.62) * mm, v(-126.48, -0.2) * mm, v(-126.48, 0) * mm]});
            skArc(sketch, "E152.0", {"start": v(-90.8, 108.11) * mm, "mid": v(-91.7, 77.84) * mm, "end": v(-104.74, 50.51) * mm});
            skFitSpline(sketch, "E153.0", {"points": [v(-126.48, 0) * mm, v(-126.48, 0.2) * mm, v(-126.48, 0.62) * mm, v(-126.45, 1.48) * mm, v(-126.37, 2.57) * mm, v(-126.23, 3.92) * mm, v(-125.95, 5.8) * mm, v(-125.44, 8.25) * mm, v(-124.57, 11.4) * mm, v(-123.44, 14.7) * mm, v(-121.62, 19.33) * mm, v(-118.77, 25.43) * mm, v(-114.67, 33.14) * mm, v(-110.1, 41.14) * mm, v(-105.34, 49.38) * mm, v(-101.43, 56.47) * mm, v(-98.47, 62.31) * mm, v(-96.37, 66.81) * mm, v(-94.44, 71.44) * mm, v(-93, 75.45) * mm, v(-92, 78.76) * mm, v(-91.33, 81.3) * mm, v(-90.75, 83.9) * mm, v(-90.35, 86.12) * mm, v(-90.1, 87.93) * mm, v(-89.88, 89.73) * mm, v(-89.7, 91.94) * mm, v(-89.6, 94.53) * mm, v(-89.61, 97.06) * mm, v(-89.72, 99.51) * mm, v(-89.98, 102.68) * mm, v(-90.47, 106.44) * mm, v(-91.26, 110.63) * mm, v(-92.14, 114.5) * mm, v(-93.04, 118.06) * mm, v(-94.2, 122.4) * mm, v(-95.17, 126.15) * mm, v(-95.82, 129.29) * mm, v(-96.14, 131.32) * mm, v(-96.3, 133.04) * mm, v(-96.31, 134.46) * mm, v(-96.23, 135.45) * mm, v(-96.11, 136.18) * mm, v(-96.02, 136.62) * mm, v(-95.93, 136.97) * mm, v(-95.85, 137.24) * mm, v(-95.76, 137.52) * mm, v(-95.62, 137.93) * mm, v(-95.4, 138.5) * mm, v(-94.93, 139.51) * mm, v(-94.14, 140.98) * mm, v(-92.83, 143) * mm, v(-91.14, 145.21) * mm, v(-89.1, 147.56) * mm, v(-86.7, 150.02) * mm, v(-83.04, 153.37) * mm, v(-77.67, 157.62) * mm, v(-70.12, 162.62) * mm, v(-61.63, 167.33) * mm, v(-52.35, 171.62) * mm, v(-42.46, 175.35) * mm, v(-32.12, 178.4) * mm, v(-23.26, 180.32) * mm, v(-16.1, 181.41) * mm, v(-10.72, 182.01) * mm, v(-6.24, 182.32) * mm, v(-2.67, 182.44) * mm, v(0, 182.47) * mm, v(2.67, 182.44) * mm, v(6.24, 182.32) * mm, v(10.72, 182.01) * mm, v(16.1, 181.41) * mm, v(23.26, 180.32) * mm, v(32.12, 178.4) * mm, v(42.46, 175.35) * mm, v(52.35, 171.62) * mm, v(61.63, 167.33) * mm, v(70.12, 162.62) * mm, v(77.67, 157.62) * mm, v(83.04, 153.37) * mm, v(86.7, 150.02) * mm, v(89.1, 147.56) * mm, v(91.14, 145.21) * mm, v(92.83, 143) * mm, v(94.14, 140.98) * mm, v(94.93, 139.51) * mm, v(95.4, 138.5) * mm, v(95.62, 137.93) * mm, v(95.76, 137.52) * mm, v(95.85, 137.24) * mm, v(95.93, 136.97) * mm, v(96.02, 136.62) * mm, v(96.11, 136.18) * mm, v(96.23, 135.45) * mm, v(96.31, 134.46) * mm, v(96.3, 133.04) * mm, v(96.14, 131.32) * mm, v(95.82, 129.29) * mm, v(95.17, 126.15) * mm, v(94.2, 122.4) * mm, v(93.04, 118.06) * mm, v(92.14, 114.5) * mm, v(91.26, 110.63) * mm, v(90.47, 106.44) * mm, v(89.98, 102.68) * mm, v(89.72, 99.51) * mm, v(89.61, 97.06) * mm, v(89.6, 94.53) * mm, v(89.7, 91.94) * mm, v(89.88, 89.73) * mm, v(90.1, 87.93) * mm, v(90.35, 86.12) * mm, v(90.75, 83.9) * mm, v(91.33, 81.3) * mm, v(92, 78.76) * mm, v(93, 75.45) * mm, v(94.44, 71.44) * mm, v(96.37, 66.81) * mm, v(98.47, 62.31) * mm, v(101.43, 56.47) * mm, v(105.34, 49.38) * mm, v(110.1, 41.14) * mm, v(114.67, 33.14) * mm, v(118.77, 25.43) * mm, v(121.62, 19.33) * mm, v(123.44, 14.7) * mm, v(124.57, 11.4) * mm, v(125.44, 8.25) * mm, v(125.95, 5.8) * mm, v(126.23, 3.92) * mm, v(126.37, 2.57) * mm, v(126.45, 1.48) * mm, v(126.48, 0.62) * mm, v(126.48, 0) * mm, v(126.48, -0.62) * mm, v(126.45, -1.48) * mm, v(126.37, -2.57) * mm, v(126.23, -3.92) * mm, v(125.95, -5.8) * mm, v(125.44, -8.25) * mm, v(124.57, -11.4) * mm, v(123.44, -14.7) * mm, v(121.62, -19.33) * mm, v(118.77, -25.43) * mm, v(114.67, -33.14) * mm, v(110.1, -41.14) * mm, v(105.34, -49.38) * mm, v(101.43, -56.47) * mm, v(98.47, -62.31) * mm, v(96.37, -66.81) * mm, v(94.44, -71.44) * mm, v(93, -75.45) * mm, v(92, -78.76) * mm, v(91.33, -81.3) * mm, v(90.75, -83.9) * mm, v(90.35, -86.12) * mm, v(90.1, -87.93) * mm, v(89.88, -89.73) * mm, v(89.7, -91.94) * mm, v(89.6, -94.53) * mm, v(89.61, -97.06) * mm, v(89.72, -99.51) * mm, v(89.98, -102.68) * mm, v(90.47, -106.44) * mm, v(91.26, -110.63) * mm, v(92.14, -114.5) * mm, v(93.04, -118.06) * mm, v(94.2, -122.4) * mm, v(95.17, -126.15) * mm, v(95.82, -129.29) * mm, v(96.14, -131.32) * mm, v(96.3, -133.04) * mm, v(96.31, -134.46) * mm, v(96.23, -135.45) * mm, v(96.11, -136.18) * mm, v(96.02, -136.62) * mm, v(95.93, -136.97) * mm, v(95.85, -137.24) * mm, v(95.76, -137.52) * mm, v(95.62, -137.93) * mm, v(95.4, -138.5) * mm, v(94.93, -139.51) * mm, v(94.14, -140.98) * mm, v(92.83, -143) * mm, v(91.14, -145.21) * mm, v(89.1, -147.56) * mm, v(86.7, -150.02) * mm, v(83.04, -153.37) * mm, v(77.67, -157.62) * mm, v(70.12, -162.62) * mm, v(61.63, -167.33) * mm, v(52.35, -171.62) * mm, v(42.46, -175.35) * mm, v(32.12, -178.4) * mm, v(23.26, -180.32) * mm, v(16.1, -181.41) * mm, v(10.72, -182.01) * mm, v(6.24, -182.32) * mm, v(2.67, -182.44) * mm, v(0, -182.47) * mm, v(-2.67, -182.44) * mm, v(-6.24, -182.32) * mm, v(-10.72, -182.01) * mm, v(-16.1, -181.41) * mm, v(-23.26, -180.32) * mm, v(-32.12, -178.4) * mm, v(-42.46, -175.35) * mm, v(-52.35, -171.62) * mm, v(-61.63, -167.33) * mm, v(-70.12, -162.62) * mm, v(-77.67, -157.62) * mm, v(-83.04, -153.37) * mm, v(-86.7, -150.02) * mm, v(-89.1, -147.56) * mm, v(-91.14, -145.21) * mm, v(-92.83, -143) * mm, v(-94.14, -140.98) * mm, v(-94.93, -139.51) * mm, v(-95.4, -138.5) * mm, v(-95.62, -137.93) * mm, v(-95.76, -137.52) * mm, v(-95.85, -137.24) * mm, v(-95.93, -136.97) * mm, v(-96.02, -136.62) * mm, v(-96.11, -136.18) * mm, v(-96.23, -135.45) * mm, v(-96.31, -134.46) * mm, v(-96.3, -133.04) * mm, v(-96.14, -131.32) * mm, v(-95.82, -129.29) * mm, v(-95.17, -126.15) * mm, v(-94.2, -122.4) * mm, v(-93.04, -118.06) * mm, v(-92.14, -114.5) * mm, v(-91.26, -110.63) * mm, v(-90.47, -106.44) * mm, v(-89.98, -102.68) * mm, v(-89.72, -99.51) * mm, v(-89.61, -97.06) * mm, v(-89.6, -94.53) * mm, v(-89.7, -91.94) * mm, v(-89.88, -89.73) * mm, v(-90.1, -87.93) * mm, v(-90.35, -86.12) * mm, v(-90.75, -83.9) * mm, v(-91.33, -81.3) * mm, v(-92, -78.76) * mm, v(-93, -75.45) * mm, v(-94.44, -71.44) * mm, v(-96.37, -66.81) * mm, v(-98.47, -62.31) * mm, v(-101.43, -56.47) * mm, v(-105.34, -49.38) * mm, v(-110.1, -41.14) * mm, v(-114.67, -33.14) * mm, v(-118.77, -25.43) * mm, v(-121.62, -19.33) * mm, v(-123.44, -14.7) * mm, v(-124.57, -11.4) * mm, v(-125.44, -8.25) * mm, v(-125.95, -5.8) * mm, v(-126.23, -3.92) * mm, v(-126.37, -2.57) * mm, v(-126.45, -1.48) * mm, v(-126.48, -0.62) * mm, v(-126.48, -0.2) * mm, v(-126.48, 0) * mm]});
            skCircle(sketch, "E154", {"center": v(-102.5, -75) * mm, "radius": 5 * mm});
            skCircle(sketch, "E155", {"center": v(0, 0) * mm, "radius": 10 * mm});
            skLineSegment(sketch, "E156", {"start": v(0, 29.34) * mm, "end": v(0, -23.66) * mm});
            skLineSegment(sketch, "E157", {"start": v(-27.56, 0) * mm, "end": v(21.08, 0) * mm, "construction": true});
            skCircle(sketch, "E158.MirrorC", {"center": v(-102.5, 75) * mm, "radius": 5 * mm});
            skCircle(sketch, "E159.MirrorC", {"center": v(102.5, 75) * mm, "radius": 5 * mm});
            skCircle(sketch, "E160.MirrorC", {"center": v(102.5, -75) * mm, "radius": 5 * mm});
            const initialGuessF4  = {"E147.0.1": [0, 0.08288104439999998, 1, 0, 0.13267715999999996, 0.11958350000000001, 0.5183294966334667, 1.2404782701353567], "E147.0.3": [0, 0.08288104439999998, 1, 0, 0.13267715999999996, 0.11958350000000001, 1.90111438345274, 2.623263156960303]};
            skSetInitialGuess(sketch, initialGuessF4);
            skSolve(sketch);
        }
        {
            var Q0;
            Q0=makeQuery(id+"F4.imprint","IMPRINT",FACE,{"disambiguationData":[TD([[makeQuery(id+"F4.imprint","IMPRINT",EDGE,{"derivedFrom":sQuery(id+"F4.wireOp",EDGE,"E154")}),1.0]])]});
            var Q1;
            Q1=makeQuery(id+"F4.imprint","IMPRINT",FACE,{"disambiguationData":[TD([[makeQuery(id+"F4.imprint","IMPRINT",EDGE,{"derivedFrom":sQuery(id+"F4.wireOp",EDGE,"E160.MirrorC")}),-1.0]])]});
            extrude(context, id + "F5", {"entities" : qUnion([Q0, Q1]), "operationType" : NewBodyOperationType.REMOVE, "endBound" : BoundingType.THROUGH_ALL, "oppositeDirection" : true, "depth" : 25 * mm, "offsetDistance" : 25 * mm});
        }
    });
